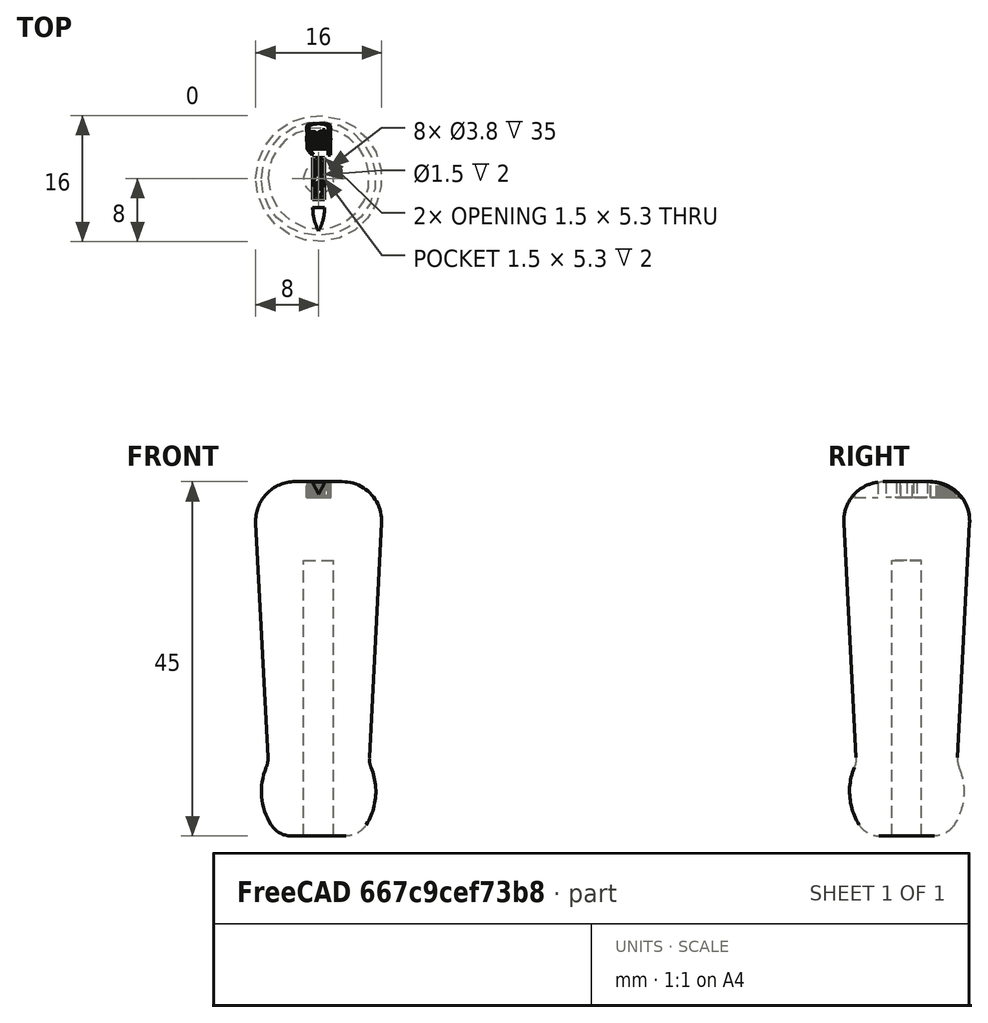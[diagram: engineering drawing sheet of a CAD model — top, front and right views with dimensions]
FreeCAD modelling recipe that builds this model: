
FCSTD DOCUMENT  (FreeCAD 1.0R39285 (Git))
Label:  NeedleFileHandle
License: All rights reserved
LicenseURL: https://en.wikipedia.org/wiki/All_rights_reserved
objects: PartDesign::CoordinateSystem×31, Sketcher::SketchObject×20, App::Part×11, Part::Part2DObjectPython×10, Part::Extrusion×10, PartDesign::Revolution×10, PartDesign::Pocket×10, PartDesign::Body×10, Part::Cut×10, App::Link×10, App::DocumentObjectGroup×3, App::FeaturePython×1, Spreadsheet::Sheet×1
note: 171 computed .brp shape members not serialized (recipe doc carries the construction recipe); baked Part::Feature solids carry a one-line shape summary decoded from their .brp

FEATURE [PartDesign::CoordinateSystem] LCS_Origin
  AttacherType = Attacher::AttachEngine3D
  AttachmentSupport = -> [X_Axis002]
  MapMode = 2
FEATURE [App::DocumentObjectGroup] Constraints
FEATURE [App::FeaturePython] Variables  # WARN: FeaturePython — macro-defined, semantics opaque (R4)
  Type = App::PropertyContainer
FEATURE [App::DocumentObjectGroup] Configurations
FEATURE [Spreadsheet::Sheet] Spreadsheet
  cells = A2='Nominal Hole Diameter; B2(NominalHoleDiameter)==3 mm; A3='Hole Tolerance; B3(HoleTolerance)==0.8 mm; A4='Hole Diameter; B4(HoleDiameter)==NominalHoleDiameter + HoleTolerance; A5='Hole Depth; B5(HoleDepth)==35 mm; A7='Bottom Flat Diameter; B7(BottomFlatDiameter)==7 mm; A9='Bottom Radius 1; B9(BottomRadius1)==3 mm; A10='Bottom Radius 2; B10(BottomRadius2)==8 mm; A11='Bottom Radius 3; B11(BottomRadius3)==BottomRadius1; A12='Top Radius; B12(TopRadius)==5 mm; A14='Top Flat Diameter; B14(TopFlatDiameter)==6 mm; A15='Top Solid Length; B15(TopSolidLength)==10 mm; A17='Bottom to Straight Height; B17(BottomToStraightHeight)==10 mm; A19='Lineup Distance; B19(LineupDistance)==20 mm; A21='Markings Depth
FEATURE [PartDesign::CoordinateSystem] LCS_Origin003
  AttacherType = Attacher::AttachEngine3D
  AttachmentSupport = -> [X_Axis006]
  MapMode = 2
FEATURE [Part::Part2DObjectPython] ShapeString002  # Draft 2D object (typed FeaturePython)
  FontFile = <userpath>/.fonts/ttf/arial.ttf
  Fuse = false
  Justification = 6
  JustificationReference = 0
  KeepLeftMargin = false
  MakeFace = true
  ObliqueAngle = 0
  ScaleToSize = true
  Size = 3
  String = 3
  Tracking = 0
FEATURE [Part::Extrusion] Extrude002  label="Text002"
  Base = -> ShapeString002
  Dir = (0,0,1)
  DirMode = 2
  FaceMakerClass = Part::FaceMakerBullseye
  FaceMakerMode = 3
  LengthFwd = 2
  LengthRev = 0
  Placement = pos=(1.5,4,43) rot=(0,0,1;1.5708rad)
  Solid = false
  Symmetric = false
FEATURE [Sketcher::SketchObject] Sketch004
  ArcFitTolerance = 1e-06
  AttachmentSupport = -> [XZ_Plane005]
  FullyConstrained = true
  MakeInternals = false
  MapMode = 5
  Placement = pos=(0,0,0) rot=(1,0,0;1.5708rad)
  expr: Constraints[10] = <<Spreadsheet>>.TopFlatDiameter / 2
  expr: Constraints[22] = <<Spreadsheet>>.TopRadius
  expr: Constraints[23] = <<Spreadsheet>>.BottomRadius1
  expr: Constraints[24] = <<Spreadsheet>>.BottomRadius2
  expr: Constraints[25] = <<Spreadsheet>>.BottomToStraightHeight
  expr: Constraints[26] = <<Spreadsheet>>.BottomFlatDiameter / 2
  expr: Constraints[27] = <<Spreadsheet>>.BottomRadius3
  expr: Constraints[5] = <<Spreadsheet>>.HoleDiameter / 2
  expr: Constraints[6] = <<Spreadsheet>>.HoleDepth
  expr: Constraints[7] = <<Spreadsheet>>.TopSolidLength
  sketch-geometry (10):
    g0: LineSegment StartX=-1.9 StartY=0 StartZ=0 EndX=-1.9 EndY=35 EndZ=0
    g1: LineSegment StartX=-1.9 StartY=35 StartZ=0 EndX=0 EndY=35 EndZ=0
    g2: LineSegment StartX=0 StartY=35 StartZ=0 EndX=0 EndY=45 EndZ=0
    g3: LineSegment StartX=0 StartY=45 StartZ=0 EndX=-3 EndY=45 EndZ=0
    g4: ArcOfCircle CenterX=-3 CenterY=40 CenterZ=0 NormalX=0 NormalY=0 NormalZ=1 AngleXU=0 Radius=5 StartAngle=1.5708 EndAngle=3.19395
    g5: LineSegment StartX=-1.9 StartY=0 StartZ=0 EndX=-3.5 EndY=0 EndZ=0
    g6: ArcOfCircle CenterX=-3.5 CenterY=3 CenterZ=0 NormalX=0 NormalY=0 NormalZ=1 AngleXU=0 Radius=3 StartAngle=3.70042 EndAngle=4.71239
    g7: ArcOfCircle CenterX=0.739385 CenterY=5.65096 CenterZ=0 NormalX=0 NormalY=0 NormalZ=1 AngleXU=0 Radius=8 StartAngle=2.75061 EndAngle=3.70042
    g8: ArcOfCircle CenterX=-9.43052 CenterY=9.84299 CenterZ=0 NormalX=0 NormalY=0 NormalZ=1 AngleXU=0 Radius=3 StartAngle=5.89221 EndAngle=6.33555
    g9: LineSegment StartX=-6.43463 StartY=10 StartZ=0 EndX=-7.99315 EndY=39.7383 EndZ=0
  constraints (28):
    c: PointOnObject(g0,g-1)
    c: Vertical(g0)
    c: Coincident(g0,g1)
    c: PointOnObject(g1,g-2)
    c: Horizontal(g1)
    c: DistanceX(g1,g1) = 1.9
    c: DistanceY(g0,g0) = 35
    c: Distance(g2) = 10
    c: Coincident(g2,g1)
    c: PointOnObject(g2,g-2)
    c: Distance(g3) = 3
    c: Coincident(g3,g2)
    c: Horizontal(g3)
    c: Coincident(g5,g0)
    c: PointOnObject(g5,g-1)
    c: Tangent(g6,g5) = 1.5708
    c: Tangent(g7,g6) = -1.5708
    c: Tangent(g8,g7) = 1.5708
    c: Tangent(g9,g8) = -1.5708
    c: Tangent(g4,g3) = -1.5708
    c: Tangent(g9,g4) = 1.5708
    c: Angle(g-2,g9) = 0.0523599
    c: Radius(g4) = 5
    c: Radius(g6) = 3
    c: Radius(g7) = 8
    c: DistanceY(g8) = 10
    c: DistanceX(g5,g-1) = 3.5
    c: Radius(g8) = 3
FEATURE [PartDesign::Revolution] Revolution002
  Angle = 360
  Angle2 = 60
  Axis = (0,2e-16,1)
  Base = (0,0,0)
  Placement = pos=(0,0,0) rot=(1,0,0;1.5708rad)
  Profile = -> Sketch004
  ReferenceAxis = -> Sketch004 [V_Axis]
  Refine = true
  Suppressed = false
  Type = 0
FEATURE [Sketcher::SketchObject] Sketch005
  ArcFitTolerance = 1e-06
  AttachmentSupport = -> [Revolution002]
  FullyConstrained = true
  MakeInternals = false
  MapMode = 5
  Placement = pos=(0,1e-14,45) rot=(0,0,1;3.14159rad)
  sketch-geometry (11):
    g0: LineSegment [constr] StartX=-0.75 StartY=-2.65 StartZ=0 EndX=0.75 EndY=-2.65 EndZ=0
    g1: LineSegment [constr] StartX=0.75 StartY=-2.65 StartZ=0 EndX=0.75 EndY=2.65 EndZ=0
    g2: LineSegment [constr] StartX=0.75 StartY=2.65 StartZ=0 EndX=-0.75 EndY=2.65 EndZ=0
    g3: LineSegment [constr] StartX=-0.75 StartY=2.65 StartZ=0 EndX=-0.75 EndY=-2.65 EndZ=0
    g4: GeomPoint [constr] X=0 Y=0 Z=0
    g5: LineSegment StartX=-0.75 StartY=3.65 StartZ=0 EndX=0.75 EndY=3.65 EndZ=0
    g6: ArcOfCircle CenterX=5.625 CenterY=3.65 CenterZ=0 NormalX=0 NormalY=0 NormalZ=1 AngleXU=0 Radius=6.375 StartAngle=2.65164 EndAngle=3.14159
    g7: ArcOfCircle CenterX=-5.625 CenterY=3.65 CenterZ=0 NormalX=0 NormalY=0 NormalZ=1 AngleXU=0 Radius=6.375 StartAngle=0 EndAngle=0.489957
    g8: ArcOfCircle CenterX=4.30667 CenterY=-7e-16 CenterZ=0 NormalX=0 NormalY=0 NormalZ=1 AngleXU=0 Radius=5.05667 StartAngle=2.58998 EndAngle=3.6932
    g9: ArcOfCircle CenterX=-4.30667 CenterY=7e-16 CenterZ=0 NormalX=0 NormalY=0 NormalZ=1 AngleXU=0 Radius=5.05667 StartAngle=5.73157 EndAngle=6.8348
    g10: GeomPoint X=0.75 Y=0 Z=0
  constraints (31):
    c: Coincident(g0,g1)
    c: Coincident(g1,g2)
    c: Coincident(g2,g3)
    c: Coincident(g3,g0)
    c: Horizontal(g0)
    c: Horizontal(g2)
    c: Vertical(g1)
    c: Vertical(g3)
    c: Symmetric(g2,g0,g4)
    c: Distance(g1,g3) = 1.5
    c: Distance(g0,g2) = 5.3
    c: Coincident(g4,g-1)
    c: Horizontal(g5)
    c: Coincident(g6,g5)
    c: PointOnObject(g6,g-2)
    c: Coincident(g7,g6)
    c: Coincident(g7,g5)
    c: Equal(g7,g6)
    c: Equal(g2,g5)
    c: Vertical(g5,g2)
    c: DistanceY(g1,g5) = 1
    c: DistanceY(g5,g6) = 3
    c: Perpendicular(g7,g5)
    c: Symmetric(g2,g2,g8)
    c: Symmetric(g0,g0,g8)
    c: Coincident(g9,g8)
    c: Coincident(g9,g8)
    c: PointOnObject(g10,g1)
    c: PointOnObject(g10,g9)
    c: PointOnObject(g10,g-1)
    c: Equal(g9,g8)
FEATURE [PartDesign::Pocket] Pocket002
  BaseFeature = -> Revolution002
  Direction = (0,0,-1)
  Length = 2
  Length2 = 5
  Placement = pos=(0,0,0) rot=(1,0,0;1.5708rad)
  Profile = -> Sketch005
  ReferenceAxis = -> Sketch005 [N_Axis]
  Refine = true
  Suppressed = false
  Type = 0
FEATURE [PartDesign::Body] Body002
  AllowCompound = false
  Group = -> [Sketch004,Revolution002,Sketch005,Pocket002]
  Origin = -> Origin005
  Tip = -> Pocket002
FEATURE [Part::Cut] Cut002
  Base = -> Body002
  Refine = true
  Tool = -> Extrude002
FEATURE [PartDesign::CoordinateSystem] Next002
  AttacherType = Attacher::AttachEngine3D
  AttachmentOffset = pos=(-20,0,0) rot=(0,0,1;3.14159rad)
  AttachmentSupport = -> [Cut002]
  MapMode = 11
  Placement = pos=(-4.2e-15,20,0) rot=(0,0,1;1.5708rad)
  expr: .AttachmentOffset.Base.x = -<<Spreadsheet>>.LineupDistance
FEATURE [PartDesign::CoordinateSystem] This002
  AttacherType = Attacher::AttachEngine3D
  AttachmentOffset = pos=(0,0,0) rot=(0,0,1;3.14159rad)
  AttachmentSupport = -> [Cut002]
  MapMode = 11
  Placement = pos=(2e-16,0,0) rot=(0,0,1;1.5708rad)
FEATURE [App::Part] Part001  label="3 - Dagger Rounded"
  Group = -> [LCS_Origin003,Body002,ShapeString002,Extrude002,Cut002,This002,Next002]
  Origin = -> Origin006
FEATURE [App::Link] ____Knife_Rounded  label="3 - Dagger Rounded001"
  AttachedBy = #This002
  AttachedTo = ____Flat_Straight#Next011
  LinkPlacement = pos=(40,-20,0) rot=(0,0,-1;1.5708rad)
  LinkedObject = -> Part001
  Placement = pos=(40,-20,0) rot=(0,0,-1;1.5708rad)
  SolverId = Asm4EE
  expr: Placement = ____Flat_Straight.Placement * Next011.Placement * AttachmentOffset * This002.Placement ^ -1
FEATURE [PartDesign::CoordinateSystem] LCS_Origin004
  AttacherType = Attacher::AttachEngine3D
  AttachmentSupport = -> [X_Axis008]
  MapMode = 2
FEATURE [Part::Part2DObjectPython] ShapeString003  # Draft 2D object (typed FeaturePython)
  FontFile = <userpath>/.fonts/ttf/arial.ttf
  Fuse = false
  Justification = 6
  JustificationReference = 0
  KeepLeftMargin = false
  MakeFace = true
  ObliqueAngle = 0
  ScaleToSize = true
  Size = 3
  String = 4
  Tracking = 0
FEATURE [Part::Extrusion] Extrude003  label="Text003"
  Base = -> ShapeString003
  Dir = (0,0,1)
  DirMode = 2
  FaceMakerClass = Part::FaceMakerBullseye
  FaceMakerMode = 3
  LengthFwd = 2
  LengthRev = 0
  Placement = pos=(1.5,4,43) rot=(0,0,1;1.5708rad)
  Solid = false
  Symmetric = false
FEATURE [Sketcher::SketchObject] Sketch006
  ArcFitTolerance = 1e-06
  AttachmentSupport = -> [XZ_Plane007]
  FullyConstrained = true
  MakeInternals = false
  MapMode = 5
  Placement = pos=(0,0,0) rot=(1,0,0;1.5708rad)
  expr: Constraints[10] = <<Spreadsheet>>.TopFlatDiameter / 2
  expr: Constraints[22] = <<Spreadsheet>>.TopRadius
  expr: Constraints[23] = <<Spreadsheet>>.BottomRadius1
  expr: Constraints[24] = <<Spreadsheet>>.BottomRadius2
  expr: Constraints[25] = <<Spreadsheet>>.BottomToStraightHeight
  expr: Constraints[26] = <<Spreadsheet>>.BottomFlatDiameter / 2
  expr: Constraints[27] = <<Spreadsheet>>.BottomRadius3
  expr: Constraints[5] = <<Spreadsheet>>.HoleDiameter / 2
  expr: Constraints[6] = <<Spreadsheet>>.HoleDepth
  expr: Constraints[7] = <<Spreadsheet>>.TopSolidLength
  sketch-geometry (10):
    g0: LineSegment StartX=-1.9 StartY=0 StartZ=0 EndX=-1.9 EndY=35 EndZ=0
    g1: LineSegment StartX=-1.9 StartY=35 StartZ=0 EndX=0 EndY=35 EndZ=0
    g2: LineSegment StartX=0 StartY=35 StartZ=0 EndX=0 EndY=45 EndZ=0
    g3: LineSegment StartX=0 StartY=45 StartZ=0 EndX=-3 EndY=45 EndZ=0
    g4: ArcOfCircle CenterX=-3 CenterY=40 CenterZ=0 NormalX=0 NormalY=0 NormalZ=1 AngleXU=0 Radius=5 StartAngle=1.5708 EndAngle=3.19395
    g5: LineSegment StartX=-1.9 StartY=0 StartZ=0 EndX=-3.5 EndY=0 EndZ=0
    g6: ArcOfCircle CenterX=-3.5 CenterY=3 CenterZ=0 NormalX=0 NormalY=0 NormalZ=1 AngleXU=0 Radius=3 StartAngle=3.70042 EndAngle=4.71239
    g7: ArcOfCircle CenterX=0.739385 CenterY=5.65096 CenterZ=0 NormalX=0 NormalY=0 NormalZ=1 AngleXU=0 Radius=8 StartAngle=2.75061 EndAngle=3.70042
    g8: ArcOfCircle CenterX=-9.43052 CenterY=9.84299 CenterZ=0 NormalX=0 NormalY=0 NormalZ=1 AngleXU=0 Radius=3 StartAngle=5.89221 EndAngle=6.33555
    g9: LineSegment StartX=-6.43463 StartY=10 StartZ=0 EndX=-7.99315 EndY=39.7383 EndZ=0
  constraints (28):
    c: PointOnObject(g0,g-1)
    c: Vertical(g0)
    c: Coincident(g0,g1)
    c: PointOnObject(g1,g-2)
    c: Horizontal(g1)
    c: DistanceX(g1,g1) = 1.9
    c: DistanceY(g0,g0) = 35
    c: Distance(g2) = 10
    c: Coincident(g2,g1)
    c: PointOnObject(g2,g-2)
    c: Distance(g3) = 3
    c: Coincident(g3,g2)
    c: Horizontal(g3)
    c: Coincident(g5,g0)
    c: PointOnObject(g5,g-1)
    c: Tangent(g6,g5) = 1.5708
    c: Tangent(g7,g6) = -1.5708
    c: Tangent(g8,g7) = 1.5708
    c: Tangent(g9,g8) = -1.5708
    c: Tangent(g4,g3) = -1.5708
    c: Tangent(g9,g4) = 1.5708
    c: Angle(g-2,g9) = 0.0523599
    c: Radius(g4) = 5
    c: Radius(g6) = 3
    c: Radius(g7) = 8
    c: DistanceY(g8) = 10
    c: DistanceX(g5,g-1) = 3.5
    c: Radius(g8) = 3
FEATURE [PartDesign::Revolution] Revolution003
  Angle = 360
  Angle2 = 60
  Axis = (0,2e-16,1)
  Base = (0,0,0)
  Placement = pos=(0,0,0) rot=(1,0,0;1.5708rad)
  Profile = -> Sketch006
  ReferenceAxis = -> Sketch006 [V_Axis]
  Refine = true
  Suppressed = false
  Type = 0
FEATURE [Sketcher::SketchObject] Sketch007
  ArcFitTolerance = 1e-06
  AttachmentSupport = -> [Revolution003]
  FullyConstrained = true
  MakeInternals = false
  MapMode = 5
  Placement = pos=(0,1e-14,45) rot=(0,0,1;3.14159rad)
  sketch-geometry (13):
    g0: LineSegment [constr] StartX=-0.75 StartY=-2.65 StartZ=0 EndX=0.75 EndY=-2.65 EndZ=0
    g1: LineSegment [constr] StartX=0.75 StartY=-2.65 StartZ=0 EndX=0.75 EndY=2.65 EndZ=0
    g2: LineSegment [constr] StartX=0.75 StartY=2.65 StartZ=0 EndX=-0.75 EndY=2.65 EndZ=0
    g3: LineSegment [constr] StartX=-0.75 StartY=2.65 StartZ=0 EndX=-0.75 EndY=-2.65 EndZ=0
    g4: GeomPoint [constr] X=0 Y=0 Z=0
    g5: LineSegment StartX=-0.75 StartY=3.65 StartZ=0 EndX=0.75 EndY=3.65 EndZ=0
    g6: ArcOfCircle CenterX=5.625 CenterY=3.65 CenterZ=0 NormalX=0 NormalY=0 NormalZ=1 AngleXU=0 Radius=6.375 StartAngle=2.65164 EndAngle=3.14159
    g7: ArcOfCircle CenterX=-5.625 CenterY=3.65 CenterZ=0 NormalX=0 NormalY=0 NormalZ=1 AngleXU=0 Radius=6.375 StartAngle=0 EndAngle=0.489957
    g8: GeomPoint X=0.75 Y=0 Z=0
    g9: ArcOfCircle CenterX=0.795417 CenterY=0 CenterZ=0 NormalX=0 NormalY=0 NormalZ=1 AngleXU=0 Radius=1.54542 StartAngle=2.11145 EndAngle=4.17174
    g10: ArcOfCircle CenterX=-0.795417 CenterY=0 CenterZ=0 NormalX=0 NormalY=0 NormalZ=1 AngleXU=0 Radius=1.54542 StartAngle=5.25304 EndAngle=7.31333
    g11: LineSegment [constr] StartX=1.393e-13 StartY=1.325 StartZ=0 EndX=0 EndY=2.65 EndZ=0
    g12: LineSegment [constr] StartX=1.393e-13 StartY=1.325 StartZ=0 EndX=0 EndY=0 EndZ=0
  constraints (36):
    c: Coincident(g0,g1)
    c: Coincident(g1,g2)
    c: Coincident(g2,g3)
    c: Coincident(g3,g0)
    c: Horizontal(g0)
    c: Horizontal(g2)
    c: Vertical(g1)
    c: Vertical(g3)
    c: Symmetric(g2,g0,g4)
    c: Distance(g1,g3) = 1.5
    c: Distance(g0,g2) = 5.3
    c: Coincident(g4,g-1)
    c: Horizontal(g5)
    c: Coincident(g6,g5)
    c: PointOnObject(g6,g-2)
    c: Coincident(g7,g6)
    c: Coincident(g7,g5)
    c: Equal(g7,g6)
    c: Equal(g2,g5)
    c: Vertical(g5,g2)
    c: DistanceY(g1,g5) = 1
    c: DistanceY(g5,g6) = 3
    c: Perpendicular(g7,g5)
    c: PointOnObject(g8,g1)
    c: PointOnObject(g8,g-1)
    c: PointOnObject(g9,g-2)
    c: Coincident(g10,g9)
    c: Coincident(g10,g9)
    c: PointOnObject(g8,g10)
    c: Symmetric(g9,g9,g4)
    c: Equal(g9,g10)
    c: Coincident(g11,g9)
    c: Symmetric(g2,g2,g11)
    c: Coincident(g12,g9)
    c: Coincident(g12,g4)
    c: Equal(g11,g12)
FEATURE [PartDesign::Pocket] Pocket003
  BaseFeature = -> Revolution003
  Direction = (0,0,-1)
  Length = 2
  Length2 = 5
  Placement = pos=(0,0,0) rot=(1,0,0;1.5708rad)
  Profile = -> Sketch007
  ReferenceAxis = -> Sketch007 [N_Axis]
  Refine = true
  Suppressed = false
  Type = 0
FEATURE [PartDesign::Body] Body003
  AllowCompound = false
  Group = -> [Sketch006,Revolution003,Sketch007,Pocket003]
  Origin = -> Origin007
  Tip = -> Pocket003
FEATURE [Part::Cut] Cut003
  Base = -> Body003
  Refine = true
  Tool = -> Extrude003
FEATURE [PartDesign::CoordinateSystem] Next003
  AttacherType = Attacher::AttachEngine3D
  AttachmentOffset = pos=(-20,0,0) rot=(0,0,1;3.14159rad)
  AttachmentSupport = -> [Cut003]
  MapMode = 11
  Placement = pos=(-4.2e-15,20,0) rot=(0,0,1;1.5708rad)
  expr: .AttachmentOffset.Base.x = -<<Spreadsheet>>.LineupDistance
FEATURE [PartDesign::CoordinateSystem] This003
  AttacherType = Attacher::AttachEngine3D
  AttachmentOffset = pos=(0,0,0) rot=(0,0,1;3.14159rad)
  AttachmentSupport = -> [Cut003]
  MapMode = 11
  Placement = pos=(2e-16,0,0) rot=(0,0,1;1.5708rad)
FEATURE [App::Part] Part002  label="4 - Dagger Rounded Small"
  Group = -> [LCS_Origin004,Body003,ShapeString003,Extrude003,Cut003,This003,Next003]
  Origin = -> Origin008
FEATURE [App::Link] ____Knife_Rounded_Small  label="4 - Dagger Rounded Small001"
  AttachedBy = #This003
  AttachedTo = ____Knife_Rounded#Next002
  LinkPlacement = pos=(60,-20,0) rot=(0,0,-1;1.5708rad)
  LinkedObject = -> Part002
  Placement = pos=(60,-20,0) rot=(0,0,-1;1.5708rad)
  SolverId = Asm4EE
  expr: Placement = ____Knife_Rounded.Placement * Next002.Placement * AttachmentOffset * This003.Placement ^ -1
FEATURE [PartDesign::CoordinateSystem] LCS_Origin005
  AttacherType = Attacher::AttachEngine3D
  AttachmentSupport = -> [X_Axis010]
  MapMode = 2
FEATURE [Part::Part2DObjectPython] ShapeString004  # Draft 2D object (typed FeaturePython)
  FontFile = <userpath>/.fonts/ttf/arial.ttf
  Fuse = false
  Justification = 6
  JustificationReference = 0
  KeepLeftMargin = false
  MakeFace = true
  ObliqueAngle = 0
  ScaleToSize = true
  Size = 3
  String = 5
  Tracking = 0
FEATURE [Part::Extrusion] Extrude004  label="Text004"
  Base = -> ShapeString004
  Dir = (0,0,1)
  DirMode = 2
  FaceMakerClass = Part::FaceMakerBullseye
  FaceMakerMode = 3
  LengthFwd = 2
  LengthRev = 0
  Placement = pos=(1.5,4,43) rot=(0,0,1;1.5708rad)
  Solid = false
  Symmetric = false
FEATURE [Sketcher::SketchObject] Sketch008
  ArcFitTolerance = 1e-06
  AttachmentSupport = -> [XZ_Plane009]
  FullyConstrained = true
  MakeInternals = false
  MapMode = 5
  Placement = pos=(0,0,0) rot=(1,0,0;1.5708rad)
  expr: Constraints[10] = <<Spreadsheet>>.TopFlatDiameter / 2
  expr: Constraints[22] = <<Spreadsheet>>.TopRadius
  expr: Constraints[23] = <<Spreadsheet>>.BottomRadius1
  expr: Constraints[24] = <<Spreadsheet>>.BottomRadius2
  expr: Constraints[25] = <<Spreadsheet>>.BottomToStraightHeight
  expr: Constraints[26] = <<Spreadsheet>>.BottomFlatDiameter / 2
  expr: Constraints[27] = <<Spreadsheet>>.BottomRadius3
  expr: Constraints[5] = <<Spreadsheet>>.HoleDiameter / 2
  expr: Constraints[6] = <<Spreadsheet>>.HoleDepth
  expr: Constraints[7] = <<Spreadsheet>>.TopSolidLength
  sketch-geometry (10):
    g0: LineSegment StartX=-1.9 StartY=0 StartZ=0 EndX=-1.9 EndY=35 EndZ=0
    g1: LineSegment StartX=-1.9 StartY=35 StartZ=0 EndX=0 EndY=35 EndZ=0
    g2: LineSegment StartX=0 StartY=35 StartZ=0 EndX=0 EndY=45 EndZ=0
    g3: LineSegment StartX=0 StartY=45 StartZ=0 EndX=-3 EndY=45 EndZ=0
    g4: ArcOfCircle CenterX=-3 CenterY=40 CenterZ=0 NormalX=0 NormalY=0 NormalZ=1 AngleXU=0 Radius=5 StartAngle=1.5708 EndAngle=3.19395
    g5: LineSegment StartX=-1.9 StartY=0 StartZ=0 EndX=-3.5 EndY=0 EndZ=0
    g6: ArcOfCircle CenterX=-3.5 CenterY=3 CenterZ=0 NormalX=0 NormalY=0 NormalZ=1 AngleXU=0 Radius=3 StartAngle=3.70042 EndAngle=4.71239
    g7: ArcOfCircle CenterX=0.739385 CenterY=5.65096 CenterZ=0 NormalX=0 NormalY=0 NormalZ=1 AngleXU=0 Radius=8 StartAngle=2.75061 EndAngle=3.70042
    g8: ArcOfCircle CenterX=-9.43052 CenterY=9.84299 CenterZ=0 NormalX=0 NormalY=0 NormalZ=1 AngleXU=0 Radius=3 StartAngle=5.89221 EndAngle=6.33555
    g9: LineSegment StartX=-6.43463 StartY=10 StartZ=0 EndX=-7.99315 EndY=39.7383 EndZ=0
  constraints (28):
    c: PointOnObject(g0,g-1)
    c: Vertical(g0)
    c: Coincident(g0,g1)
    c: PointOnObject(g1,g-2)
    c: Horizontal(g1)
    c: DistanceX(g1,g1) = 1.9
    c: DistanceY(g0,g0) = 35
    c: Distance(g2) = 10
    c: Coincident(g2,g1)
    c: PointOnObject(g2,g-2)
    c: Distance(g3) = 3
    c: Coincident(g3,g2)
    c: Horizontal(g3)
    c: Coincident(g5,g0)
    c: PointOnObject(g5,g-1)
    c: Tangent(g6,g5) = 1.5708
    c: Tangent(g7,g6) = -1.5708
    c: Tangent(g8,g7) = 1.5708
    c: Tangent(g9,g8) = -1.5708
    c: Tangent(g4,g3) = -1.5708
    c: Tangent(g9,g4) = 1.5708
    c: Angle(g-2,g9) = 0.0523599
    c: Radius(g4) = 5
    c: Radius(g6) = 3
    c: Radius(g7) = 8
    c: DistanceY(g8) = 10
    c: DistanceX(g5,g-1) = 3.5
    c: Radius(g8) = 3
FEATURE [PartDesign::Revolution] Revolution004
  Angle = 360
  Angle2 = 60
  Axis = (0,2e-16,1)
  Base = (0,0,0)
  Placement = pos=(0,0,0) rot=(1,0,0;1.5708rad)
  Profile = -> Sketch008
  ReferenceAxis = -> Sketch008 [V_Axis]
  Refine = true
  Suppressed = false
  Type = 0
FEATURE [Sketcher::SketchObject] Sketch009
  ArcFitTolerance = 1e-06
  AttachmentSupport = -> [Revolution004]
  FullyConstrained = true
  MakeInternals = false
  MapMode = 5
  Placement = pos=(0,1e-14,45) rot=(0,0,1;3.14159rad)
  sketch-geometry (12):
    g0: LineSegment [constr] StartX=-0.75 StartY=-2.65 StartZ=0 EndX=0.75 EndY=-2.65 EndZ=0
    g1: LineSegment [constr] StartX=0.75 StartY=-2.65 StartZ=0 EndX=0.75 EndY=2.65 EndZ=0
    g2: LineSegment [constr] StartX=0.75 StartY=2.65 StartZ=0 EndX=-0.75 EndY=2.65 EndZ=0
    g3: LineSegment [constr] StartX=-0.75 StartY=2.65 StartZ=0 EndX=-0.75 EndY=-2.65 EndZ=0
    g4: GeomPoint [constr] X=0 Y=0 Z=0
    g5: LineSegment StartX=-0.75 StartY=3.65 StartZ=0 EndX=0.75 EndY=3.65 EndZ=0
    g6: ArcOfCircle CenterX=5.625 CenterY=3.65 CenterZ=0 NormalX=0 NormalY=0 NormalZ=1 AngleXU=0 Radius=6.375 StartAngle=2.65164 EndAngle=3.14159
    g7: ArcOfCircle CenterX=-5.625 CenterY=3.65 CenterZ=0 NormalX=0 NormalY=0 NormalZ=1 AngleXU=0 Radius=6.375 StartAngle=1e-16 EndAngle=0.489957
    g8: GeomPoint X=0.75 Y=0 Z=0
    g9: LineSegment StartX=0.75 StartY=2.65 StartZ=0 EndX=0.75 EndY=-2.65 EndZ=0
    g10: LineSegment StartX=0.75 StartY=-2.65 StartZ=0 EndX=-0.75 EndY=0 EndZ=0
    g11: LineSegment StartX=-0.75 StartY=0 StartZ=0 EndX=0.75 EndY=2.65 EndZ=0
  constraints (31):
    c: Coincident(g0,g1)
    c: Coincident(g1,g2)
    c: Coincident(g2,g3)
    c: Coincident(g3,g0)
    c: Horizontal(g0)
    c: Horizontal(g2)
    c: Vertical(g1)
    c: Vertical(g3)
    c: Symmetric(g2,g0,g4)
    c: Distance(g1,g3) = 1.5
    c: Distance(g0,g2) = 5.3
    c: Coincident(g4,g-1)
    c: Horizontal(g5)
    c: Coincident(g6,g5)
    c: PointOnObject(g6,g-2)
    c: Coincident(g7,g6)
    c: Coincident(g7,g5)
    c: Equal(g7,g6)
    c: Equal(g2,g5)
    c: Vertical(g5,g2)
    c: DistanceY(g1,g5) = 1
    c: DistanceY(g5,g6) = 3
    c: Perpendicular(g7,g5)
    c: PointOnObject(g8,g1)
    c: PointOnObject(g8,g-1)
    c: Coincident(g9,g10)
    c: Symmetric(g3,g3,g10)
    c: Coincident(g10,g11)
    c: Coincident(g11,g9)
    c: Coincident(g9,g0)
    c: Coincident(g9,g1)
FEATURE [PartDesign::Pocket] Pocket004
  BaseFeature = -> Revolution004
  Direction = (0,0,-1)
  Length = 2
  Length2 = 5
  Placement = pos=(0,0,0) rot=(1,0,0;1.5708rad)
  Profile = -> Sketch009
  ReferenceAxis = -> Sketch009 [N_Axis]
  Refine = true
  Suppressed = false
  Type = 0
FEATURE [PartDesign::Body] Body004
  AllowCompound = false
  Group = -> [Sketch008,Revolution004,Sketch009,Pocket004]
  Origin = -> Origin009
  Tip = -> Pocket004
FEATURE [Part::Cut] Cut004
  Base = -> Body004
  Refine = true
  Tool = -> Extrude004
FEATURE [PartDesign::CoordinateSystem] Next004
  AttacherType = Attacher::AttachEngine3D
  AttachmentOffset = pos=(-20,0,0) rot=(0,0,1;3.14159rad)
  AttachmentSupport = -> [Cut004]
  MapMode = 11
  Placement = pos=(-4.2e-15,20,0) rot=(0,0,1;1.5708rad)
  expr: .AttachmentOffset.Base.x = -<<Spreadsheet>>.LineupDistance
FEATURE [PartDesign::CoordinateSystem] This004
  AttacherType = Attacher::AttachEngine3D
  AttachmentOffset = pos=(0,0,0) rot=(0,0,1;3.14159rad)
  AttachmentSupport = -> [Cut004]
  MapMode = 11
  Placement = pos=(2e-16,0,0) rot=(0,0,1;1.5708rad)
FEATURE [App::Part] Part003  label="5 - Triangle Flattened"
  Group = -> [LCS_Origin005,Body004,ShapeString004,Extrude004,Cut004,This004,Next004]
  Origin = -> Origin010
FEATURE [App::Link] ____Triangle_Flattened  label="5 - Triangle Flattened001"
  AttachedBy = #This004
  AttachedTo = ____Knife_Rounded_Small#Next003
  LinkPlacement = pos=(80,-20,0) rot=(0,0,-1;1.5708rad)
  LinkedObject = -> Part003
  Placement = pos=(80,-20,0) rot=(0,0,-1;1.5708rad)
  SolverId = Asm4EE
  expr: Placement = ____Knife_Rounded_Small.Placement * Next003.Placement * AttachmentOffset * This004.Placement ^ -1
FEATURE [PartDesign::CoordinateSystem] LCS_Origin006
  AttacherType = Attacher::AttachEngine3D
  AttachmentSupport = -> [X_Axis012]
  MapMode = 2
FEATURE [Part::Part2DObjectPython] ShapeString005  # Draft 2D object (typed FeaturePython)
  FontFile = <userpath>/.fonts/ttf/arial.ttf
  Fuse = false
  Justification = 6
  JustificationReference = 0
  KeepLeftMargin = false
  MakeFace = true
  ObliqueAngle = 0
  ScaleToSize = true
  Size = 3
  String = 6
  Tracking = 0
FEATURE [Part::Extrusion] Extrude005  label="Text005"
  Base = -> ShapeString005
  Dir = (0,0,1)
  DirMode = 2
  FaceMakerClass = Part::FaceMakerBullseye
  FaceMakerMode = 3
  LengthFwd = 2
  LengthRev = 0
  Placement = pos=(1.5,4,43) rot=(0,0,1;1.5708rad)
  Solid = false
  Symmetric = false
FEATURE [Sketcher::SketchObject] Sketch010
  ArcFitTolerance = 1e-06
  AttachmentSupport = -> [XZ_Plane011]
  FullyConstrained = true
  MakeInternals = false
  MapMode = 5
  Placement = pos=(0,0,0) rot=(1,0,0;1.5708rad)
  expr: Constraints[10] = <<Spreadsheet>>.TopFlatDiameter / 2
  expr: Constraints[22] = <<Spreadsheet>>.TopRadius
  expr: Constraints[23] = <<Spreadsheet>>.BottomRadius1
  expr: Constraints[24] = <<Spreadsheet>>.BottomRadius2
  expr: Constraints[25] = <<Spreadsheet>>.BottomToStraightHeight
  expr: Constraints[26] = <<Spreadsheet>>.BottomFlatDiameter / 2
  expr: Constraints[27] = <<Spreadsheet>>.BottomRadius3
  expr: Constraints[5] = <<Spreadsheet>>.HoleDiameter / 2
  expr: Constraints[6] = <<Spreadsheet>>.HoleDepth
  expr: Constraints[7] = <<Spreadsheet>>.TopSolidLength
  sketch-geometry (10):
    g0: LineSegment StartX=-1.9 StartY=0 StartZ=0 EndX=-1.9 EndY=35 EndZ=0
    g1: LineSegment StartX=-1.9 StartY=35 StartZ=0 EndX=0 EndY=35 EndZ=0
    g2: LineSegment StartX=0 StartY=35 StartZ=0 EndX=0 EndY=45 EndZ=0
    g3: LineSegment StartX=0 StartY=45 StartZ=0 EndX=-3 EndY=45 EndZ=0
    g4: ArcOfCircle CenterX=-3 CenterY=40 CenterZ=0 NormalX=0 NormalY=0 NormalZ=1 AngleXU=0 Radius=5 StartAngle=1.5708 EndAngle=3.19395
    g5: LineSegment StartX=-1.9 StartY=0 StartZ=0 EndX=-3.5 EndY=0 EndZ=0
    g6: ArcOfCircle CenterX=-3.5 CenterY=3 CenterZ=0 NormalX=0 NormalY=0 NormalZ=1 AngleXU=0 Radius=3 StartAngle=3.70042 EndAngle=4.71239
    g7: ArcOfCircle CenterX=0.739385 CenterY=5.65096 CenterZ=0 NormalX=0 NormalY=0 NormalZ=1 AngleXU=0 Radius=8 StartAngle=2.75061 EndAngle=3.70042
    g8: ArcOfCircle CenterX=-9.43052 CenterY=9.84299 CenterZ=0 NormalX=0 NormalY=0 NormalZ=1 AngleXU=0 Radius=3 StartAngle=5.89221 EndAngle=6.33555
    g9: LineSegment StartX=-6.43463 StartY=10 StartZ=0 EndX=-7.99315 EndY=39.7383 EndZ=0
  constraints (28):
    c: PointOnObject(g0,g-1)
    c: Vertical(g0)
    c: Coincident(g0,g1)
    c: PointOnObject(g1,g-2)
    c: Horizontal(g1)
    c: DistanceX(g1,g1) = 1.9
    c: DistanceY(g0,g0) = 35
    c: Distance(g2) = 10
    c: Coincident(g2,g1)
    c: PointOnObject(g2,g-2)
    c: Distance(g3) = 3
    c: Coincident(g3,g2)
    c: Horizontal(g3)
    c: Coincident(g5,g0)
    c: PointOnObject(g5,g-1)
    c: Tangent(g6,g5) = 1.5708
    c: Tangent(g7,g6) = -1.5708
    c: Tangent(g8,g7) = 1.5708
    c: Tangent(g9,g8) = -1.5708
    c: Tangent(g4,g3) = -1.5708
    c: Tangent(g9,g4) = 1.5708
    c: Angle(g-2,g9) = 0.0523599
    c: Radius(g4) = 5
    c: Radius(g6) = 3
    c: Radius(g7) = 8
    c: DistanceY(g8) = 10
    c: DistanceX(g5,g-1) = 3.5
    c: Radius(g8) = 3
FEATURE [PartDesign::Revolution] Revolution005
  Angle = 360
  Angle2 = 60
  Axis = (0,2e-16,1)
  Base = (0,0,0)
  Placement = pos=(0,0,0) rot=(1,0,0;1.5708rad)
  Profile = -> Sketch010
  ReferenceAxis = -> Sketch010 [V_Axis]
  Refine = true
  Suppressed = false
  Type = 0
FEATURE [Sketcher::SketchObject] Sketch011
  ArcFitTolerance = 1e-06
  AttachmentSupport = -> [Revolution005]
  FullyConstrained = true
  MakeInternals = false
  MapMode = 5
  Placement = pos=(0,1e-14,45) rot=(0,0,1;3.14159rad)
  sketch-geometry (12):
    g0: LineSegment [constr] StartX=-0.75 StartY=-2.65 StartZ=0 EndX=0.75 EndY=-2.65 EndZ=0
    g1: LineSegment [constr] StartX=0.75 StartY=-2.65 StartZ=0 EndX=0.75 EndY=2.65 EndZ=0
    g2: LineSegment [constr] StartX=0.75 StartY=2.65 StartZ=0 EndX=-0.75 EndY=2.65 EndZ=0
    g3: LineSegment [constr] StartX=-0.75 StartY=2.65 StartZ=0 EndX=-0.75 EndY=-2.65 EndZ=0
    g4: GeomPoint [constr] X=0 Y=0 Z=0
    g5: LineSegment StartX=-0.75 StartY=3.65 StartZ=0 EndX=0.75 EndY=3.65 EndZ=0
    g6: ArcOfCircle CenterX=5.625 CenterY=3.65 CenterZ=0 NormalX=0 NormalY=0 NormalZ=1 AngleXU=0 Radius=6.375 StartAngle=2.65164 EndAngle=3.14159
    g7: ArcOfCircle CenterX=-5.625 CenterY=3.65 CenterZ=0 NormalX=0 NormalY=0 NormalZ=1 AngleXU=0 Radius=6.375 StartAngle=0 EndAngle=0.489957
    g8: GeomPoint X=0.75 Y=0 Z=0
    g9: LineSegment StartX=-0.75 StartY=1.325 StartZ=0 EndX=0.75 EndY=1.325 EndZ=0
    g10: LineSegment StartX=0.75 StartY=1.325 StartZ=0 EndX=0 EndY=-2.65 EndZ=0
    g11: LineSegment StartX=0 StartY=-2.65 StartZ=0 EndX=-0.75 EndY=1.325 EndZ=0
  constraints (32):
    c: Coincident(g0,g1)
    c: Coincident(g1,g2)
    c: Coincident(g2,g3)
    c: Coincident(g3,g0)
    c: Horizontal(g0)
    c: Horizontal(g2)
    c: Vertical(g1)
    c: Vertical(g3)
    c: Symmetric(g2,g0,g4)
    c: Distance(g1,g3) = 1.5
    c: Distance(g0,g2) = 5.3
    c: Coincident(g4,g-1)
    c: Horizontal(g5)
    c: Coincident(g6,g5)
    c: PointOnObject(g6,g-2)
    c: Coincident(g7,g6)
    c: Coincident(g7,g5)
    c: Equal(g7,g6)
    c: Equal(g2,g5)
    c: Vertical(g5,g2)
    c: DistanceY(g1,g5) = 1
    c: DistanceY(g5,g6) = 3
    c: Perpendicular(g7,g5)
    c: PointOnObject(g8,g1)
    c: PointOnObject(g8,g-1)
    c: PointOnObject(g9,g3)
    c: Horizontal(g9)
    c: Coincident(g9,g10)
    c: Symmetric(g0,g0,g10)
    c: Coincident(g10,g11)
    c: Coincident(g11,g9)
    c: Symmetric(g8,g1,g9)
FEATURE [PartDesign::Pocket] Pocket005
  BaseFeature = -> Revolution005
  Direction = (0,0,-1)
  Length = 2
  Length2 = 5
  Placement = pos=(0,0,0) rot=(1,0,0;1.5708rad)
  Profile = -> Sketch011
  ReferenceAxis = -> Sketch011 [N_Axis]
  Refine = true
  Suppressed = false
  Type = 0
FEATURE [PartDesign::Body] Body005
  AllowCompound = false
  Group = -> [Sketch010,Revolution005,Sketch011,Pocket005]
  Origin = -> Origin011
  Tip = -> Pocket005
FEATURE [Part::Cut] Cut005
  Base = -> Body005
  Refine = true
  Tool = -> Extrude005
FEATURE [PartDesign::CoordinateSystem] Next005
  AttacherType = Attacher::AttachEngine3D
  AttachmentOffset = pos=(-20,0,0) rot=(0,0,1;3.14159rad)
  AttachmentSupport = -> [Cut005]
  MapMode = 11
  Placement = pos=(-4.2e-15,20,0) rot=(0,0,1;1.5708rad)
  expr: .AttachmentOffset.Base.x = -<<Spreadsheet>>.LineupDistance
FEATURE [PartDesign::CoordinateSystem] This005
  AttacherType = Attacher::AttachEngine3D
  AttachmentOffset = pos=(0,0,0) rot=(0,0,1;3.14159rad)
  AttachmentSupport = -> [Cut005]
  MapMode = 11
  Placement = pos=(2e-16,0,0) rot=(0,0,1;1.5708rad)
FEATURE [App::Part] Part004  label="6 - Knife"
  Group = -> [LCS_Origin006,Body005,ShapeString005,Extrude005,Cut005,This005,Next005]
  Origin = -> Origin012
FEATURE [App::Link] ____Sharp_Edge  label="6 - Knife001"
  AttachedBy = #This005
  AttachedTo = Parent Assembly#LCS_Origin
  AttachmentOffset = pos=(0,-40,0) rot=(0,0,1;0rad)
  LinkPlacement = pos=(0,-40,0) rot=(0,0,-1;1.5708rad)
  LinkedObject = -> Part004
  Placement = pos=(0,-40,0) rot=(0,0,-1;1.5708rad)
  SolverId = Asm4EE
  expr: Placement = LCS_Origin.Placement * AttachmentOffset * This005.Placement ^ -1
FEATURE [PartDesign::CoordinateSystem] LCS_Origin007
  AttacherType = Attacher::AttachEngine3D
  AttachmentSupport = -> [X_Axis014]
  MapMode = 2
FEATURE [Part::Part2DObjectPython] ShapeString006  # Draft 2D object (typed FeaturePython)
  FontFile = <userpath>/.fonts/ttf/arial.ttf
  Fuse = false
  Justification = 6
  JustificationReference = 0
  KeepLeftMargin = false
  MakeFace = true
  ObliqueAngle = 0
  ScaleToSize = true
  Size = 3
  String = 7
  Tracking = 0
FEATURE [Part::Extrusion] Extrude006  label="Text006"
  Base = -> ShapeString006
  Dir = (0,0,1)
  DirMode = 2
  FaceMakerClass = Part::FaceMakerBullseye
  FaceMakerMode = 3
  LengthFwd = 2
  LengthRev = 0
  Placement = pos=(1.5,4,43) rot=(0,0,1;1.5708rad)
  Solid = false
  Symmetric = false
FEATURE [Sketcher::SketchObject] Sketch012
  ArcFitTolerance = 1e-06
  AttachmentSupport = -> [XZ_Plane013]
  FullyConstrained = true
  MakeInternals = false
  MapMode = 5
  Placement = pos=(0,0,0) rot=(1,0,0;1.5708rad)
  expr: Constraints[10] = <<Spreadsheet>>.TopFlatDiameter / 2
  expr: Constraints[22] = <<Spreadsheet>>.TopRadius
  expr: Constraints[23] = <<Spreadsheet>>.BottomRadius1
  expr: Constraints[24] = <<Spreadsheet>>.BottomRadius2
  expr: Constraints[25] = <<Spreadsheet>>.BottomToStraightHeight
  expr: Constraints[26] = <<Spreadsheet>>.BottomFlatDiameter / 2
  expr: Constraints[27] = <<Spreadsheet>>.BottomRadius3
  expr: Constraints[5] = <<Spreadsheet>>.HoleDiameter / 2
  expr: Constraints[6] = <<Spreadsheet>>.HoleDepth
  expr: Constraints[7] = <<Spreadsheet>>.TopSolidLength
  sketch-geometry (10):
    g0: LineSegment StartX=-1.9 StartY=0 StartZ=0 EndX=-1.9 EndY=35 EndZ=0
    g1: LineSegment StartX=-1.9 StartY=35 StartZ=0 EndX=0 EndY=35 EndZ=0
    g2: LineSegment StartX=0 StartY=35 StartZ=0 EndX=0 EndY=45 EndZ=0
    g3: LineSegment StartX=0 StartY=45 StartZ=0 EndX=-3 EndY=45 EndZ=0
    g4: ArcOfCircle CenterX=-3 CenterY=40 CenterZ=0 NormalX=0 NormalY=0 NormalZ=1 AngleXU=0 Radius=5 StartAngle=1.5708 EndAngle=3.19395
    g5: LineSegment StartX=-1.9 StartY=0 StartZ=0 EndX=-3.5 EndY=0 EndZ=0
    g6: ArcOfCircle CenterX=-3.5 CenterY=3 CenterZ=0 NormalX=0 NormalY=0 NormalZ=1 AngleXU=0 Radius=3 StartAngle=3.70042 EndAngle=4.71239
    g7: ArcOfCircle CenterX=0.739385 CenterY=5.65096 CenterZ=0 NormalX=0 NormalY=0 NormalZ=1 AngleXU=0 Radius=8 StartAngle=2.75061 EndAngle=3.70042
    g8: ArcOfCircle CenterX=-9.43052 CenterY=9.84299 CenterZ=0 NormalX=0 NormalY=0 NormalZ=1 AngleXU=0 Radius=3 StartAngle=5.89221 EndAngle=6.33555
    g9: LineSegment StartX=-6.43463 StartY=10 StartZ=0 EndX=-7.99315 EndY=39.7383 EndZ=0
  constraints (28):
    c: PointOnObject(g0,g-1)
    c: Vertical(g0)
    c: Coincident(g0,g1)
    c: PointOnObject(g1,g-2)
    c: Horizontal(g1)
    c: DistanceX(g1,g1) = 1.9
    c: DistanceY(g0,g0) = 35
    c: Distance(g2) = 10
    c: Coincident(g2,g1)
    c: PointOnObject(g2,g-2)
    c: Distance(g3) = 3
    c: Coincident(g3,g2)
    c: Horizontal(g3)
    c: Coincident(g5,g0)
    c: PointOnObject(g5,g-1)
    c: Tangent(g6,g5) = 1.5708
    c: Tangent(g7,g6) = -1.5708
    c: Tangent(g8,g7) = 1.5708
    c: Tangent(g9,g8) = -1.5708
    c: Tangent(g4,g3) = -1.5708
    c: Tangent(g9,g4) = 1.5708
    c: Angle(g-2,g9) = 0.0523599
    c: Radius(g4) = 5
    c: Radius(g6) = 3
    c: Radius(g7) = 8
    c: DistanceY(g8) = 10
    c: DistanceX(g5,g-1) = 3.5
    c: Radius(g8) = 3
FEATURE [PartDesign::Revolution] Revolution006
  Angle = 360
  Angle2 = 60
  Axis = (0,2e-16,1)
  Base = (0,0,0)
  Placement = pos=(0,0,0) rot=(1,0,0;1.5708rad)
  Profile = -> Sketch012
  ReferenceAxis = -> Sketch012 [V_Axis]
  Refine = true
  Suppressed = false
  Type = 0
FEATURE [Sketcher::SketchObject] Sketch013
  ArcFitTolerance = 1e-06
  AttachmentSupport = -> [Revolution006]
  FullyConstrained = true
  MakeInternals = false
  MapMode = 5
  Placement = pos=(0,1e-14,45) rot=(0,0,1;3.14159rad)
  sketch-geometry (10):
    g0: LineSegment [constr] StartX=-0.75 StartY=-2.65 StartZ=0 EndX=0.75 EndY=-2.65 EndZ=0
    g1: LineSegment [constr] StartX=0.75 StartY=-2.65 StartZ=0 EndX=0.75 EndY=2.65 EndZ=0
    g2: LineSegment [constr] StartX=0.75 StartY=2.65 StartZ=0 EndX=-0.75 EndY=2.65 EndZ=0
    g3: LineSegment [constr] StartX=-0.75 StartY=2.65 StartZ=0 EndX=-0.75 EndY=-2.65 EndZ=0
    g4: GeomPoint [constr] X=0 Y=0 Z=0
    g5: LineSegment StartX=-0.75 StartY=3.65 StartZ=0 EndX=0.75 EndY=3.65 EndZ=0
    g6: ArcOfCircle CenterX=5.625 CenterY=3.65 CenterZ=0 NormalX=0 NormalY=0 NormalZ=1 AngleXU=0 Radius=6.375 StartAngle=2.65164 EndAngle=3.14159
    g7: ArcOfCircle CenterX=-5.625 CenterY=3.65 CenterZ=0 NormalX=0 NormalY=0 NormalZ=1 AngleXU=0 Radius=6.375 StartAngle=0 EndAngle=0.489957
    g8: GeomPoint X=0.75 Y=0 Z=0
    g9: Circle CenterX=0 CenterY=0 CenterZ=0 NormalX=0 NormalY=0 NormalZ=1 AngleXU=0 Radius=0.75
  constraints (27):
    c: Coincident(g0,g1)
    c: Coincident(g1,g2)
    c: Coincident(g2,g3)
    c: Coincident(g3,g0)
    c: Horizontal(g0)
    c: Horizontal(g2)
    c: Vertical(g1)
    c: Vertical(g3)
    c: Symmetric(g2,g0,g4)
    c: Distance(g1,g3) = 1.5
    c: Distance(g0,g2) = 5.3
    c: Coincident(g4,g-1)
    c: Horizontal(g5)
    c: Coincident(g6,g5)
    c: PointOnObject(g6,g-2)
    c: Coincident(g7,g6)
    c: Coincident(g7,g5)
    c: Equal(g7,g6)
    c: Equal(g2,g5)
    c: Vertical(g5,g2)
    c: DistanceY(g1,g5) = 1
    c: DistanceY(g5,g6) = 3
    c: Perpendicular(g7,g5)
    c: PointOnObject(g8,g1)
    c: PointOnObject(g8,g-1)
    c: Coincident(g9,g4)
    c: PointOnObject(g8,g9)
FEATURE [PartDesign::Pocket] Pocket006
  BaseFeature = -> Revolution006
  Direction = (0,0,-1)
  Length = 2
  Length2 = 5
  Placement = pos=(0,0,0) rot=(1,0,0;1.5708rad)
  Profile = -> Sketch013
  ReferenceAxis = -> Sketch013 [N_Axis]
  Refine = true
  Suppressed = false
  Type = 0
FEATURE [PartDesign::Body] Body006
  AllowCompound = false
  Group = -> [Sketch012,Revolution006,Sketch013,Pocket006]
  Origin = -> Origin013
  Tip = -> Pocket006
FEATURE [Part::Cut] Cut006
  Base = -> Body006
  Refine = true
  Tool = -> Extrude006
FEATURE [PartDesign::CoordinateSystem] Next006
  AttacherType = Attacher::AttachEngine3D
  AttachmentOffset = pos=(-20,0,0) rot=(0,0,1;3.14159rad)
  AttachmentSupport = -> [Cut006]
  MapMode = 11
  Placement = pos=(-4.2e-15,20,0) rot=(0,0,1;1.5708rad)
  expr: .AttachmentOffset.Base.x = -<<Spreadsheet>>.LineupDistance
FEATURE [PartDesign::CoordinateSystem] This006
  AttacherType = Attacher::AttachEngine3D
  AttachmentOffset = pos=(0,0,0) rot=(0,0,1;3.14159rad)
  AttachmentSupport = -> [Cut006]
  MapMode = 11
  Placement = pos=(2e-16,0,0) rot=(0,0,1;1.5708rad)
FEATURE [App::Part] Part005  label="7 - Round"
  Group = -> [LCS_Origin007,Body006,ShapeString006,Extrude006,Cut006,This006,Next006]
  Origin = -> Origin014
FEATURE [App::Link] ____Round  label="7 - Round001"
  AttachedBy = #This006
  AttachedTo = ____Sharp_Edge#Next005
  LinkPlacement = pos=(20,-40,0) rot=(0,0,-1;1.5708rad)
  LinkedObject = -> Part005
  Placement = pos=(20,-40,0) rot=(0,0,-1;1.5708rad)
  SolverId = Asm4EE
  expr: Placement = ____Sharp_Edge.Placement * Next005.Placement * AttachmentOffset * This006.Placement ^ -1
FEATURE [PartDesign::CoordinateSystem] LCS_Origin008
  AttacherType = Attacher::AttachEngine3D
  AttachmentSupport = -> [X_Axis016]
  MapMode = 2
FEATURE [Part::Part2DObjectPython] ShapeString007  # Draft 2D object (typed FeaturePython)
  FontFile = <userpath>/.fonts/ttf/arial.ttf
  Fuse = false
  Justification = 6
  JustificationReference = 0
  KeepLeftMargin = false
  MakeFace = true
  ObliqueAngle = 0
  ScaleToSize = true
  Size = 3
  String = 8
  Tracking = 0
FEATURE [Part::Extrusion] Extrude007  label="Text007"
  Base = -> ShapeString007
  Dir = (0,0,1)
  DirMode = 2
  FaceMakerClass = Part::FaceMakerBullseye
  FaceMakerMode = 3
  LengthFwd = 2
  LengthRev = 0
  Placement = pos=(1.5,4,43) rot=(0,0,1;1.5708rad)
  Solid = false
  Symmetric = false
FEATURE [Sketcher::SketchObject] Sketch014
  ArcFitTolerance = 1e-06
  AttachmentSupport = -> [XZ_Plane015]
  FullyConstrained = true
  MakeInternals = false
  MapMode = 5
  Placement = pos=(0,0,0) rot=(1,0,0;1.5708rad)
  expr: Constraints[10] = <<Spreadsheet>>.TopFlatDiameter / 2
  expr: Constraints[22] = <<Spreadsheet>>.TopRadius
  expr: Constraints[23] = <<Spreadsheet>>.BottomRadius1
  expr: Constraints[24] = <<Spreadsheet>>.BottomRadius2
  expr: Constraints[25] = <<Spreadsheet>>.BottomToStraightHeight
  expr: Constraints[26] = <<Spreadsheet>>.BottomFlatDiameter / 2
  expr: Constraints[27] = <<Spreadsheet>>.BottomRadius3
  expr: Constraints[5] = <<Spreadsheet>>.HoleDiameter / 2
  expr: Constraints[6] = <<Spreadsheet>>.HoleDepth
  expr: Constraints[7] = <<Spreadsheet>>.TopSolidLength
  sketch-geometry (10):
    g0: LineSegment StartX=-1.9 StartY=0 StartZ=0 EndX=-1.9 EndY=35 EndZ=0
    g1: LineSegment StartX=-1.9 StartY=35 StartZ=0 EndX=0 EndY=35 EndZ=0
    g2: LineSegment StartX=0 StartY=35 StartZ=0 EndX=0 EndY=45 EndZ=0
    g3: LineSegment StartX=0 StartY=45 StartZ=0 EndX=-3 EndY=45 EndZ=0
    g4: ArcOfCircle CenterX=-3 CenterY=40 CenterZ=0 NormalX=0 NormalY=0 NormalZ=1 AngleXU=0 Radius=5 StartAngle=1.5708 EndAngle=3.19395
    g5: LineSegment StartX=-1.9 StartY=0 StartZ=0 EndX=-3.5 EndY=0 EndZ=0
    g6: ArcOfCircle CenterX=-3.5 CenterY=3 CenterZ=0 NormalX=0 NormalY=0 NormalZ=1 AngleXU=0 Radius=3 StartAngle=3.70042 EndAngle=4.71239
    g7: ArcOfCircle CenterX=0.739385 CenterY=5.65096 CenterZ=0 NormalX=0 NormalY=0 NormalZ=1 AngleXU=0 Radius=8 StartAngle=2.75061 EndAngle=3.70042
    g8: ArcOfCircle CenterX=-9.43052 CenterY=9.84299 CenterZ=0 NormalX=0 NormalY=0 NormalZ=1 AngleXU=0 Radius=3 StartAngle=5.89221 EndAngle=6.33555
    g9: LineSegment StartX=-6.43463 StartY=10 StartZ=0 EndX=-7.99315 EndY=39.7383 EndZ=0
  constraints (28):
    c: PointOnObject(g0,g-1)
    c: Vertical(g0)
    c: Coincident(g0,g1)
    c: PointOnObject(g1,g-2)
    c: Horizontal(g1)
    c: DistanceX(g1,g1) = 1.9
    c: DistanceY(g0,g0) = 35
    c: Distance(g2) = 10
    c: Coincident(g2,g1)
    c: PointOnObject(g2,g-2)
    c: Distance(g3) = 3
    c: Coincident(g3,g2)
    c: Horizontal(g3)
    c: Coincident(g5,g0)
    c: PointOnObject(g5,g-1)
    c: Tangent(g6,g5) = 1.5708
    c: Tangent(g7,g6) = -1.5708
    c: Tangent(g8,g7) = 1.5708
    c: Tangent(g9,g8) = -1.5708
    c: Tangent(g4,g3) = -1.5708
    c: Tangent(g9,g4) = 1.5708
    c: Angle(g-2,g9) = 0.0523599
    c: Radius(g4) = 5
    c: Radius(g6) = 3
    c: Radius(g7) = 8
    c: DistanceY(g8) = 10
    c: DistanceX(g5,g-1) = 3.5
    c: Radius(g8) = 3
FEATURE [PartDesign::Revolution] Revolution007
  Angle = 360
  Angle2 = 60
  Axis = (0,2e-16,1)
  Base = (0,0,0)
  Placement = pos=(0,0,0) rot=(1,0,0;1.5708rad)
  Profile = -> Sketch014
  ReferenceAxis = -> Sketch014 [V_Axis]
  Refine = true
  Suppressed = false
  Type = 0
FEATURE [Sketcher::SketchObject] Sketch015
  ArcFitTolerance = 1e-06
  AttachmentSupport = -> [Revolution007]
  FullyConstrained = true
  MakeInternals = false
  MapMode = 5
  Placement = pos=(0,1e-14,45) rot=(0,0,1;3.14159rad)
  sketch-geometry (12):
    g0: LineSegment [constr] StartX=-0.75 StartY=-2.65 StartZ=0 EndX=0.75 EndY=-2.65 EndZ=0
    g1: LineSegment [constr] StartX=0.75 StartY=-2.65 StartZ=0 EndX=0.75 EndY=2.65 EndZ=0
    g2: LineSegment [constr] StartX=0.75 StartY=2.65 StartZ=0 EndX=-0.75 EndY=2.65 EndZ=0
    g3: LineSegment [constr] StartX=-0.75 StartY=2.65 StartZ=0 EndX=-0.75 EndY=-2.65 EndZ=0
    g4: GeomPoint [constr] X=0 Y=0 Z=0
    g5: LineSegment StartX=-0.75 StartY=3.65 StartZ=0 EndX=0.75 EndY=3.65 EndZ=0
    g6: ArcOfCircle CenterX=5.625 CenterY=3.65 CenterZ=0 NormalX=0 NormalY=0 NormalZ=1 AngleXU=0 Radius=6.375 StartAngle=2.65164 EndAngle=3.14159
    g7: ArcOfCircle CenterX=-5.625 CenterY=3.65 CenterZ=0 NormalX=0 NormalY=0 NormalZ=1 AngleXU=0 Radius=6.375 StartAngle=0 EndAngle=0.489957
    g8: GeomPoint X=0.75 Y=0 Z=0
    g9: LineSegment StartX=-0.75 StartY=1e-16 StartZ=0 EndX=0.75 EndY=0.866025 EndZ=0
    g10: LineSegment StartX=0.75 StartY=0.866025 StartZ=0 EndX=0.75 EndY=-0.866025 EndZ=0
    g11: LineSegment StartX=0.75 StartY=-0.866025 StartZ=0 EndX=-0.75 EndY=1e-16 EndZ=0
  constraints (33):
    c: Coincident(g0,g1)
    c: Coincident(g1,g2)
    c: Coincident(g2,g3)
    c: Coincident(g3,g0)
    c: Horizontal(g0)
    c: Horizontal(g2)
    c: Vertical(g1)
    c: Vertical(g3)
    c: Symmetric(g2,g0,g4)
    c: Distance(g1,g3) = 1.5
    c: Distance(g0,g2) = 5.3
    c: Coincident(g4,g-1)
    c: Horizontal(g5)
    c: Coincident(g6,g5)
    c: PointOnObject(g6,g-2)
    c: Coincident(g7,g6)
    c: Coincident(g7,g5)
    c: Equal(g7,g6)
    c: Equal(g2,g5)
    c: Vertical(g5,g2)
    c: DistanceY(g1,g5) = 1
    c: DistanceY(g5,g6) = 3
    c: Perpendicular(g7,g5)
    c: PointOnObject(g8,g1)
    c: PointOnObject(g8,g-1)
    c: Symmetric(g3,g3,g9)
    c: PointOnObject(g9,g1)
    c: Coincident(g9,g10)
    c: PointOnObject(g10,g1)
    c: Coincident(g10,g11)
    c: Coincident(g11,g9)
    c: Equal(g9,g10)
    c: Equal(g10,g11)
FEATURE [PartDesign::Pocket] Pocket007
  BaseFeature = -> Revolution007
  Direction = (0,0,-1)
  Length = 2
  Length2 = 5
  Placement = pos=(0,0,0) rot=(1,0,0;1.5708rad)
  Profile = -> Sketch015
  ReferenceAxis = -> Sketch015 [N_Axis]
  Refine = true
  Suppressed = false
  Type = 0
FEATURE [PartDesign::Body] Body007
  AllowCompound = false
  Group = -> [Sketch014,Revolution007,Sketch015,Pocket007]
  Origin = -> Origin015
  Tip = -> Pocket007
FEATURE [Part::Cut] Cut007
  Base = -> Body007
  Refine = true
  Tool = -> Extrude007
FEATURE [PartDesign::CoordinateSystem] Next007
  AttacherType = Attacher::AttachEngine3D
  AttachmentOffset = pos=(-20,0,0) rot=(0,0,1;3.14159rad)
  AttachmentSupport = -> [Cut007]
  MapMode = 11
  Placement = pos=(-4.2e-15,20,0) rot=(0,0,1;1.5708rad)
  expr: .AttachmentOffset.Base.x = -<<Spreadsheet>>.LineupDistance
FEATURE [PartDesign::CoordinateSystem] This007
  AttacherType = Attacher::AttachEngine3D
  AttachmentOffset = pos=(0,0,0) rot=(0,0,1;3.14159rad)
  AttachmentSupport = -> [Cut007]
  MapMode = 11
  Placement = pos=(2e-16,0,0) rot=(0,0,1;1.5708rad)
FEATURE [App::Part] Part006  label="8 - Triangle"
  Group = -> [LCS_Origin008,Body007,ShapeString007,Extrude007,Cut007,This007,Next007]
  Origin = -> Origin016
FEATURE [App::Link] ____Triangle  label="8 - Triangle001"
  AttachedBy = #This007
  AttachedTo = ____Round#Next006
  LinkPlacement = pos=(40,-40,0) rot=(0,0,-1;1.5708rad)
  LinkedObject = -> Part006
  Placement = pos=(40,-40,0) rot=(0,0,-1;1.5708rad)
  SolverId = Asm4EE
  expr: Placement = ____Round.Placement * Next006.Placement * AttachmentOffset * This007.Placement ^ -1
FEATURE [PartDesign::CoordinateSystem] LCS_Origin009
  AttacherType = Attacher::AttachEngine3D
  AttachmentSupport = -> [X_Axis018]
  MapMode = 2
FEATURE [Part::Part2DObjectPython] ShapeString008  # Draft 2D object (typed FeaturePython)
  FontFile = <userpath>/.fonts/ttf/arial.ttf
  Fuse = false
  Justification = 6
  JustificationReference = 0
  KeepLeftMargin = false
  MakeFace = true
  ObliqueAngle = 0
  ScaleToSize = true
  Size = 3
  String = 9
  Tracking = 0
FEATURE [Part::Extrusion] Extrude008  label="Text008"
  Base = -> ShapeString008
  Dir = (0,0,1)
  DirMode = 2
  FaceMakerClass = Part::FaceMakerBullseye
  FaceMakerMode = 3
  LengthFwd = 2
  LengthRev = 0
  Placement = pos=(1.5,4,43) rot=(0,0,1;1.5708rad)
  Solid = false
  Symmetric = false
FEATURE [Sketcher::SketchObject] Sketch016
  ArcFitTolerance = 1e-06
  AttachmentSupport = -> [XZ_Plane017]
  FullyConstrained = true
  MakeInternals = false
  MapMode = 5
  Placement = pos=(0,0,0) rot=(1,0,0;1.5708rad)
  expr: Constraints[10] = <<Spreadsheet>>.TopFlatDiameter / 2
  expr: Constraints[22] = <<Spreadsheet>>.TopRadius
  expr: Constraints[23] = <<Spreadsheet>>.BottomRadius1
  expr: Constraints[24] = <<Spreadsheet>>.BottomRadius2
  expr: Constraints[25] = <<Spreadsheet>>.BottomToStraightHeight
  expr: Constraints[26] = <<Spreadsheet>>.BottomFlatDiameter / 2
  expr: Constraints[27] = <<Spreadsheet>>.BottomRadius3
  expr: Constraints[5] = <<Spreadsheet>>.HoleDiameter / 2
  expr: Constraints[6] = <<Spreadsheet>>.HoleDepth
  expr: Constraints[7] = <<Spreadsheet>>.TopSolidLength
  sketch-geometry (10):
    g0: LineSegment StartX=-1.9 StartY=0 StartZ=0 EndX=-1.9 EndY=35 EndZ=0
    g1: LineSegment StartX=-1.9 StartY=35 StartZ=0 EndX=0 EndY=35 EndZ=0
    g2: LineSegment StartX=0 StartY=35 StartZ=0 EndX=0 EndY=45 EndZ=0
    g3: LineSegment StartX=0 StartY=45 StartZ=0 EndX=-3 EndY=45 EndZ=0
    g4: ArcOfCircle CenterX=-3 CenterY=40 CenterZ=0 NormalX=0 NormalY=0 NormalZ=1 AngleXU=0 Radius=5 StartAngle=1.5708 EndAngle=3.19395
    g5: LineSegment StartX=-1.9 StartY=0 StartZ=0 EndX=-3.5 EndY=0 EndZ=0
    g6: ArcOfCircle CenterX=-3.5 CenterY=3 CenterZ=0 NormalX=0 NormalY=0 NormalZ=1 AngleXU=0 Radius=3 StartAngle=3.70042 EndAngle=4.71239
    g7: ArcOfCircle CenterX=0.739385 CenterY=5.65096 CenterZ=0 NormalX=0 NormalY=0 NormalZ=1 AngleXU=0 Radius=8 StartAngle=2.75061 EndAngle=3.70042
    g8: ArcOfCircle CenterX=-9.43052 CenterY=9.84299 CenterZ=0 NormalX=0 NormalY=0 NormalZ=1 AngleXU=0 Radius=3 StartAngle=5.89221 EndAngle=6.33555
    g9: LineSegment StartX=-6.43463 StartY=10 StartZ=0 EndX=-7.99315 EndY=39.7383 EndZ=0
  constraints (28):
    c: PointOnObject(g0,g-1)
    c: Vertical(g0)
    c: Coincident(g0,g1)
    c: PointOnObject(g1,g-2)
    c: Horizontal(g1)
    c: DistanceX(g1,g1) = 1.9
    c: DistanceY(g0,g0) = 35
    c: Distance(g2) = 10
    c: Coincident(g2,g1)
    c: PointOnObject(g2,g-2)
    c: Distance(g3) = 3
    c: Coincident(g3,g2)
    c: Horizontal(g3)
    c: Coincident(g5,g0)
    c: PointOnObject(g5,g-1)
    c: Tangent(g6,g5) = 1.5708
    c: Tangent(g7,g6) = -1.5708
    c: Tangent(g8,g7) = 1.5708
    c: Tangent(g9,g8) = -1.5708
    c: Tangent(g4,g3) = -1.5708
    c: Tangent(g9,g4) = 1.5708
    c: Angle(g-2,g9) = 0.0523599
    c: Radius(g4) = 5
    c: Radius(g6) = 3
    c: Radius(g7) = 8
    c: DistanceY(g8) = 10
    c: DistanceX(g5,g-1) = 3.5
    c: Radius(g8) = 3
FEATURE [PartDesign::Revolution] Revolution008
  Angle = 360
  Angle2 = 60
  Axis = (0,2e-16,1)
  Base = (0,0,0)
  Placement = pos=(0,0,0) rot=(1,0,0;1.5708rad)
  Profile = -> Sketch016
  ReferenceAxis = -> Sketch016 [V_Axis]
  Refine = true
  Suppressed = false
  Type = 0
FEATURE [Sketcher::SketchObject] Sketch017
  ArcFitTolerance = 1e-06
  AttachmentSupport = -> [Revolution008]
  FullyConstrained = true
  MakeInternals = false
  MapMode = 5
  Placement = pos=(0,1e-14,45) rot=(0,0,1;3.14159rad)
  sketch-geometry (14):
    g0: LineSegment [constr] StartX=-0.75 StartY=-2.65 StartZ=0 EndX=0.75 EndY=-2.65 EndZ=0
    g1: LineSegment [constr] StartX=0.75 StartY=-2.65 StartZ=0 EndX=0.75 EndY=2.65 EndZ=0
    g2: LineSegment [constr] StartX=0.75 StartY=2.65 StartZ=0 EndX=-0.75 EndY=2.65 EndZ=0
    g3: LineSegment [constr] StartX=-0.75 StartY=2.65 StartZ=0 EndX=-0.75 EndY=-2.65 EndZ=0
    g4: GeomPoint [constr] X=0 Y=0 Z=0
    g5: LineSegment StartX=-0.75 StartY=3.65 StartZ=0 EndX=0.75 EndY=3.65 EndZ=0
    g6: ArcOfCircle CenterX=5.625 CenterY=3.65 CenterZ=0 NormalX=0 NormalY=0 NormalZ=1 AngleXU=0 Radius=6.375 StartAngle=2.65164 EndAngle=3.14159
    g7: ArcOfCircle CenterX=-5.625 CenterY=3.65 CenterZ=0 NormalX=0 NormalY=0 NormalZ=1 AngleXU=0 Radius=6.375 StartAngle=0 EndAngle=0.489957
    g8: GeomPoint X=0.75 Y=0 Z=0
    g9: LineSegment StartX=-0.75 StartY=0.75 StartZ=0 EndX=-0.75 EndY=-0.75 EndZ=0
    g10: LineSegment StartX=-0.75 StartY=-0.75 StartZ=0 EndX=0.75 EndY=-0.75 EndZ=0
    g11: LineSegment StartX=0.75 StartY=-0.75 StartZ=0 EndX=0.75 EndY=0.75 EndZ=0
    g12: LineSegment StartX=0.75 StartY=0.75 StartZ=0 EndX=-0.75 EndY=0.75 EndZ=0
    g13: GeomPoint [constr] X=0 Y=0 Z=0
  constraints (37):
    c: Coincident(g0,g1)
    c: Coincident(g1,g2)
    c: Coincident(g2,g3)
    c: Coincident(g3,g0)
    c: Horizontal(g0)
    c: Horizontal(g2)
    c: Vertical(g1)
    c: Vertical(g3)
    c: Symmetric(g2,g0,g4)
    c: Distance(g1,g3) = 1.5
    c: Distance(g0,g2) = 5.3
    c: Coincident(g4,g-1)
    c: Horizontal(g5)
    c: Coincident(g6,g5)
    c: PointOnObject(g6,g-2)
    c: Coincident(g7,g6)
    c: Coincident(g7,g5)
    c: Equal(g7,g6)
    c: Equal(g2,g5)
    c: Vertical(g5,g2)
    c: DistanceY(g1,g5) = 1
    c: DistanceY(g5,g6) = 3
    c: Perpendicular(g7,g5)
    c: PointOnObject(g8,g1)
    c: PointOnObject(g8,g-1)
    c: Coincident(g9,g10)
    c: Coincident(g10,g11)
    c: Coincident(g11,g12)
    c: Coincident(g12,g9)
    c: Vertical(g9)
    c: Vertical(g11)
    c: Horizontal(g10)
    c: Horizontal(g12)
    c: Symmetric(g11,g9,g13)
    c: Coincident(g13,g4)
    c: PointOnObject(g10,g1)
    c: Equal(g11,g12)
FEATURE [PartDesign::Pocket] Pocket008
  BaseFeature = -> Revolution008
  Direction = (0,0,-1)
  Length = 2
  Length2 = 5
  Placement = pos=(0,0,0) rot=(1,0,0;1.5708rad)
  Profile = -> Sketch017
  ReferenceAxis = -> Sketch017 [N_Axis]
  Refine = true
  Suppressed = false
  Type = 0
FEATURE [PartDesign::Body] Body008
  AllowCompound = false
  Group = -> [Sketch016,Revolution008,Sketch017,Pocket008]
  Origin = -> Origin017
  Tip = -> Pocket008
FEATURE [Part::Cut] Cut008
  Base = -> Body008
  Refine = true
  Tool = -> Extrude008
FEATURE [PartDesign::CoordinateSystem] Next008
  AttacherType = Attacher::AttachEngine3D
  AttachmentOffset = pos=(-20,0,0) rot=(0,0,1;3.14159rad)
  AttachmentSupport = -> [Cut008]
  MapMode = 11
  Placement = pos=(-4.2e-15,20,0) rot=(0,0,1;1.5708rad)
  expr: .AttachmentOffset.Base.x = -<<Spreadsheet>>.LineupDistance
FEATURE [PartDesign::CoordinateSystem] This008
  AttacherType = Attacher::AttachEngine3D
  AttachmentOffset = pos=(0,0,0) rot=(0,0,1;3.14159rad)
  AttachmentSupport = -> [Cut008]
  MapMode = 11
  Placement = pos=(2e-16,0,0) rot=(0,0,1;1.5708rad)
FEATURE [App::Part] Part007  label="9 - Square"
  Group = -> [LCS_Origin009,Body008,ShapeString008,Extrude008,Cut008,This008,Next008]
  Origin = -> Origin018
FEATURE [App::Link] ____Square  label="9 - Square001"
  AttachedBy = #This008
  AttachedTo = ____Triangle#Next007
  LinkPlacement = pos=(60,-40,0) rot=(0,0,-1;1.5708rad)
  LinkedObject = -> Part007
  Placement = pos=(60,-40,0) rot=(0,0,-1;1.5708rad)
  SolverId = Asm4EE
  expr: Placement = ____Triangle.Placement * Next007.Placement * AttachmentOffset * This008.Placement ^ -1
FEATURE [PartDesign::CoordinateSystem] LCS_Origin010
  AttacherType = Attacher::AttachEngine3D
  AttachmentSupport = -> [X_Axis020]
  MapMode = 2
FEATURE [Part::Part2DObjectPython] ShapeString009  # Draft 2D object (typed FeaturePython)
  FontFile = <userpath>/.fonts/ttf/arial.ttf
  Fuse = false
  Justification = 6
  JustificationReference = 0
  KeepLeftMargin = false
  MakeFace = true
  ObliqueAngle = 0
  ScaleToSize = true
  Size = 3
  String = 10
  Tracking = 0
FEATURE [Part::Extrusion] Extrude009  label="Text009"
  Base = -> ShapeString009
  Dir = (0,0,1)
  DirMode = 2
  FaceMakerClass = Part::FaceMakerBullseye
  FaceMakerMode = 3
  LengthFwd = 2
  LengthRev = 0
  Placement = pos=(1.5,3,43) rot=(0,0,1;1.5708rad)
  Solid = false
  Symmetric = false
FEATURE [Sketcher::SketchObject] Sketch018
  ArcFitTolerance = 1e-06
  AttachmentSupport = -> [XZ_Plane019]
  FullyConstrained = true
  MakeInternals = false
  MapMode = 5
  Placement = pos=(0,0,0) rot=(1,0,0;1.5708rad)
  expr: Constraints[10] = <<Spreadsheet>>.TopFlatDiameter / 2
  expr: Constraints[22] = <<Spreadsheet>>.TopRadius
  expr: Constraints[23] = <<Spreadsheet>>.BottomRadius1
  expr: Constraints[24] = <<Spreadsheet>>.BottomRadius2
  expr: Constraints[25] = <<Spreadsheet>>.BottomToStraightHeight
  expr: Constraints[26] = <<Spreadsheet>>.BottomFlatDiameter / 2
  expr: Constraints[27] = <<Spreadsheet>>.BottomRadius3
  expr: Constraints[5] = <<Spreadsheet>>.HoleDiameter / 2
  expr: Constraints[6] = <<Spreadsheet>>.HoleDepth
  expr: Constraints[7] = <<Spreadsheet>>.TopSolidLength
  sketch-geometry (10):
    g0: LineSegment StartX=-1.9 StartY=0 StartZ=0 EndX=-1.9 EndY=35 EndZ=0
    g1: LineSegment StartX=-1.9 StartY=35 StartZ=0 EndX=0 EndY=35 EndZ=0
    g2: LineSegment StartX=0 StartY=35 StartZ=0 EndX=0 EndY=45 EndZ=0
    g3: LineSegment StartX=0 StartY=45 StartZ=0 EndX=-3 EndY=45 EndZ=0
    g4: ArcOfCircle CenterX=-3 CenterY=40 CenterZ=0 NormalX=0 NormalY=0 NormalZ=1 AngleXU=0 Radius=5 StartAngle=1.5708 EndAngle=3.19395
    g5: LineSegment StartX=-1.9 StartY=0 StartZ=0 EndX=-3.5 EndY=0 EndZ=0
    g6: ArcOfCircle CenterX=-3.5 CenterY=3 CenterZ=0 NormalX=0 NormalY=0 NormalZ=1 AngleXU=0 Radius=3 StartAngle=3.70042 EndAngle=4.71239
    g7: ArcOfCircle CenterX=0.739385 CenterY=5.65096 CenterZ=0 NormalX=0 NormalY=0 NormalZ=1 AngleXU=0 Radius=8 StartAngle=2.75061 EndAngle=3.70042
    g8: ArcOfCircle CenterX=-9.43052 CenterY=9.84299 CenterZ=0 NormalX=0 NormalY=0 NormalZ=1 AngleXU=0 Radius=3 StartAngle=5.89221 EndAngle=6.33555
    g9: LineSegment StartX=-6.43463 StartY=10 StartZ=0 EndX=-7.99315 EndY=39.7383 EndZ=0
  constraints (28):
    c: PointOnObject(g0,g-1)
    c: Vertical(g0)
    c: Coincident(g0,g1)
    c: PointOnObject(g1,g-2)
    c: Horizontal(g1)
    c: DistanceX(g1,g1) = 1.9
    c: DistanceY(g0,g0) = 35
    c: Distance(g2) = 10
    c: Coincident(g2,g1)
    c: PointOnObject(g2,g-2)
    c: Distance(g3) = 3
    c: Coincident(g3,g2)
    c: Horizontal(g3)
    c: Coincident(g5,g0)
    c: PointOnObject(g5,g-1)
    c: Tangent(g6,g5) = 1.5708
    c: Tangent(g7,g6) = -1.5708
    c: Tangent(g8,g7) = 1.5708
    c: Tangent(g9,g8) = -1.5708
    c: Tangent(g4,g3) = -1.5708
    c: Tangent(g9,g4) = 1.5708
    c: Angle(g-2,g9) = 0.0523599
    c: Radius(g4) = 5
    c: Radius(g6) = 3
    c: Radius(g7) = 8
    c: DistanceY(g8) = 10
    c: DistanceX(g5,g-1) = 3.5
    c: Radius(g8) = 3
FEATURE [PartDesign::Revolution] Revolution009
  Angle = 360
  Angle2 = 60
  Axis = (0,2e-16,1)
  Base = (0,0,0)
  Placement = pos=(0,0,0) rot=(1,0,0;1.5708rad)
  Profile = -> Sketch018
  ReferenceAxis = -> Sketch018 [V_Axis]
  Refine = true
  Suppressed = false
  Type = 0
FEATURE [Sketcher::SketchObject] Sketch019
  ArcFitTolerance = 1e-06
  AttachmentSupport = -> [Revolution009]
  FullyConstrained = true
  MakeInternals = false
  MapMode = 5
  Placement = pos=(0,1e-14,45) rot=(0,0,1;3.14159rad)
  sketch-geometry (12):
    g0: LineSegment [constr] StartX=-0.75 StartY=-2.65 StartZ=0 EndX=0.75 EndY=-2.65 EndZ=0
    g1: LineSegment [constr] StartX=0.75 StartY=-2.65 StartZ=0 EndX=0.75 EndY=2.65 EndZ=0
    g2: LineSegment [constr] StartX=0.75 StartY=2.65 StartZ=0 EndX=-0.75 EndY=2.65 EndZ=0
    g3: LineSegment [constr] StartX=-0.75 StartY=2.65 StartZ=0 EndX=-0.75 EndY=-2.65 EndZ=0
    g4: GeomPoint [constr] X=0 Y=0 Z=0
    g5: LineSegment StartX=-0.75 StartY=3.65 StartZ=0 EndX=0.75 EndY=3.65 EndZ=0
    g6: ArcOfCircle CenterX=5.625 CenterY=3.65 CenterZ=0 NormalX=0 NormalY=0 NormalZ=1 AngleXU=0 Radius=6.375 StartAngle=2.65164 EndAngle=3.14159
    g7: ArcOfCircle CenterX=-5.625 CenterY=3.65 CenterZ=0 NormalX=0 NormalY=0 NormalZ=1 AngleXU=0 Radius=6.375 StartAngle=0 EndAngle=0.489957
    g8: GeomPoint X=0.75 Y=0 Z=0
    g9: GeomPoint [constr] X=0 Y=0 Z=0
    g10: ArcOfCircle CenterX=-2.34083 CenterY=0 CenterZ=0 NormalX=0 NormalY=0 NormalZ=1 AngleXU=0 Radius=3.09083 StartAngle=5.25304 EndAngle=7.31333
    g11: LineSegment StartX=-0.75 StartY=-2.65 StartZ=0 EndX=-0.75 EndY=2.65 EndZ=0
  constraints (32):
    c: Coincident(g0,g1)
    c: Coincident(g1,g2)
    c: Coincident(g2,g3)
    c: Coincident(g3,g0)
    c: Horizontal(g0)
    c: Horizontal(g2)
    c: Vertical(g1)
    c: Vertical(g3)
    c: Symmetric(g2,g0,g4)
    c: Distance(g1,g3) = 1.5
    c: Distance(g0,g2) = 5.3
    c: Coincident(g4,g-1)
    c: Horizontal(g5)
    c: Coincident(g6,g5)
    c: PointOnObject(g6,g-2)
    c: Coincident(g7,g6)
    c: Coincident(g7,g5)
    c: Equal(g7,g6)
    c: Equal(g2,g5)
    c: Vertical(g5,g2)
    c: DistanceY(g1,g5) = 1
    c: DistanceY(g5,g6) = 3
    c: Perpendicular(g7,g5)
    c: PointOnObject(g8,g1)
    c: PointOnObject(g8,g-1)
    c: Coincident(g9,g4)
    c: PointOnObject(g10,g3)
    c: PointOnObject(g8,g10)
    c: PointOnObject(g10,g-1)
    c: Coincident(g11,g10)
    c: Coincident(g11,g10)
    c: Coincident(g10,g2)
FEATURE [PartDesign::Pocket] Pocket009
  BaseFeature = -> Revolution009
  Direction = (0,0,-1)
  Length = 2
  Length2 = 5
  Placement = pos=(0,0,0) rot=(1,0,0;1.5708rad)
  Profile = -> Sketch019
  ReferenceAxis = -> Sketch019 [N_Axis]
  Refine = true
  Suppressed = false
  Type = 0
FEATURE [PartDesign::Body] Body009
  AllowCompound = false
  Group = -> [Sketch018,Revolution009,Sketch019,Pocket009]
  Origin = -> Origin019
  Tip = -> Pocket009
FEATURE [Part::Cut] Cut009
  Base = -> Body009
  Refine = true
  Tool = -> Extrude009
FEATURE [PartDesign::CoordinateSystem] Next009
  AttacherType = Attacher::AttachEngine3D
  AttachmentOffset = pos=(-20,0,0) rot=(0,0,1;3.14159rad)
  AttachmentSupport = -> [Cut009]
  MapMode = 11
  Placement = pos=(-4.2e-15,20,0) rot=(0,0,1;1.5708rad)
  expr: .AttachmentOffset.Base.x = -<<Spreadsheet>>.LineupDistance
FEATURE [PartDesign::CoordinateSystem] This009
  AttacherType = Attacher::AttachEngine3D
  AttachmentOffset = pos=(0,0,0) rot=(0,0,1;3.14159rad)
  AttachmentSupport = -> [Cut009]
  MapMode = 11
  Placement = pos=(2e-16,0,0) rot=(0,0,1;1.5708rad)
FEATURE [App::Part] Part008  label="10 - Half Round"
  Group = -> [LCS_Origin010,Body009,ShapeString009,Extrude009,Cut009,This009,Next009]
  Origin = -> Origin020
FEATURE [App::Link] _0___Half_Round  label="10 - Half Round001"
  AttachedBy = #This009
  AttachedTo = ____Square#Next008
  LinkPlacement = pos=(80,-40,0) rot=(0,0,-1;1.5708rad)
  LinkedObject = -> Part008
  Placement = pos=(80,-40,0) rot=(0,0,-1;1.5708rad)
  SolverId = Asm4EE
  expr: Placement = ____Square.Placement * Next008.Placement * AttachmentOffset * This009.Placement ^ -1
FEATURE [PartDesign::CoordinateSystem] LCS_Origin011
  AttacherType = Attacher::AttachEngine3D
  AttachmentSupport = -> [X_Axis022]
  MapMode = 2
FEATURE [Part::Part2DObjectPython] ShapeString010  # Draft 2D object (typed FeaturePython)
  FontFile = <userpath>/.fonts/ttf/arial.ttf
  Fuse = false
  Justification = 6
  JustificationReference = 0
  KeepLeftMargin = false
  MakeFace = true
  ObliqueAngle = 0
  ScaleToSize = true
  Size = 3
  String = 1
  Tracking = 0
FEATURE [Part::Extrusion] Extrude010  label="Text010"
  Base = -> ShapeString010
  Dir = (0,0,1)
  DirMode = 2
  FaceMakerClass = Part::FaceMakerBullseye
  FaceMakerMode = 3
  LengthFwd = 2
  LengthRev = 0
  Placement = pos=(1.5,4,43) rot=(0,0,1;1.5708rad)
  Solid = false
  Symmetric = false
FEATURE [Sketcher::SketchObject] Sketch020
  ArcFitTolerance = 1e-06
  AttachmentSupport = -> [XZ_Plane021]
  FullyConstrained = true
  MakeInternals = false
  MapMode = 5
  Placement = pos=(0,0,0) rot=(1,0,0;1.5708rad)
  expr: Constraints[10] = <<Spreadsheet>>.TopFlatDiameter / 2
  expr: Constraints[22] = <<Spreadsheet>>.TopRadius
  expr: Constraints[23] = <<Spreadsheet>>.BottomRadius1
  expr: Constraints[24] = <<Spreadsheet>>.BottomRadius2
  expr: Constraints[25] = <<Spreadsheet>>.BottomToStraightHeight
  expr: Constraints[26] = <<Spreadsheet>>.BottomFlatDiameter / 2
  expr: Constraints[27] = <<Spreadsheet>>.BottomRadius3
  expr: Constraints[5] = <<Spreadsheet>>.HoleDiameter / 2
  expr: Constraints[6] = <<Spreadsheet>>.HoleDepth
  expr: Constraints[7] = <<Spreadsheet>>.TopSolidLength
  sketch-geometry (10):
    g0: LineSegment StartX=-1.9 StartY=0 StartZ=0 EndX=-1.9 EndY=35 EndZ=0
    g1: LineSegment StartX=-1.9 StartY=35 StartZ=0 EndX=0 EndY=35 EndZ=0
    g2: LineSegment StartX=0 StartY=35 StartZ=0 EndX=0 EndY=45 EndZ=0
    g3: LineSegment StartX=0 StartY=45 StartZ=0 EndX=-3 EndY=45 EndZ=0
    g4: ArcOfCircle CenterX=-3 CenterY=40 CenterZ=0 NormalX=0 NormalY=0 NormalZ=1 AngleXU=0 Radius=5 StartAngle=1.5708 EndAngle=3.19395
    g5: LineSegment StartX=-1.9 StartY=0 StartZ=0 EndX=-3.5 EndY=0 EndZ=0
    g6: ArcOfCircle CenterX=-3.5 CenterY=3 CenterZ=0 NormalX=0 NormalY=0 NormalZ=1 AngleXU=0 Radius=3 StartAngle=3.70042 EndAngle=4.71239
    g7: ArcOfCircle CenterX=0.739385 CenterY=5.65096 CenterZ=0 NormalX=0 NormalY=0 NormalZ=1 AngleXU=0 Radius=8 StartAngle=2.75061 EndAngle=3.70042
    g8: ArcOfCircle CenterX=-9.43052 CenterY=9.84299 CenterZ=0 NormalX=0 NormalY=0 NormalZ=1 AngleXU=0 Radius=3 StartAngle=5.89221 EndAngle=6.33555
    g9: LineSegment StartX=-6.43463 StartY=10 StartZ=0 EndX=-7.99315 EndY=39.7383 EndZ=0
  constraints (28):
    c: PointOnObject(g0,g-1)
    c: Vertical(g0)
    c: Coincident(g0,g1)
    c: PointOnObject(g1,g-2)
    c: Horizontal(g1)
    c: DistanceX(g1,g1) = 1.9
    c: DistanceY(g0,g0) = 35
    c: Distance(g2) = 10
    c: Coincident(g2,g1)
    c: PointOnObject(g2,g-2)
    c: Distance(g3) = 3
    c: Coincident(g3,g2)
    c: Horizontal(g3)
    c: Coincident(g5,g0)
    c: PointOnObject(g5,g-1)
    c: Tangent(g6,g5) = 1.5708
    c: Tangent(g7,g6) = -1.5708
    c: Tangent(g8,g7) = 1.5708
    c: Tangent(g9,g8) = -1.5708
    c: Tangent(g4,g3) = -1.5708
    c: Tangent(g9,g4) = 1.5708
    c: Angle(g-2,g9) = 0.0523599
    c: Radius(g4) = 5
    c: Radius(g6) = 3
    c: Radius(g7) = 8
    c: DistanceY(g8) = 10
    c: DistanceX(g5,g-1) = 3.5
    c: Radius(g8) = 3
FEATURE [PartDesign::Revolution] Revolution010
  Angle = 360
  Angle2 = 60
  Axis = (0,2e-16,1)
  Base = (0,0,0)
  Placement = pos=(0,0,0) rot=(1,0,0;1.5708rad)
  Profile = -> Sketch020
  ReferenceAxis = -> Sketch020 [V_Axis]
  Refine = true
  Suppressed = false
  Type = 0
FEATURE [Sketcher::SketchObject] Sketch021
  ArcFitTolerance = 1e-06
  AttachmentSupport = -> [Revolution010]
  FullyConstrained = true
  MakeInternals = false
  MapMode = 5
  Placement = pos=(0,1e-14,45) rot=(0,0,1;3.14159rad)
  sketch-geometry (8):
    g0: LineSegment StartX=-0.75 StartY=-2.65 StartZ=0 EndX=0.75 EndY=-2.65 EndZ=0
    g1: LineSegment StartX=0.75 StartY=-2.65 StartZ=0 EndX=0.75 EndY=2.65 EndZ=0
    g2: LineSegment StartX=0.75 StartY=2.65 StartZ=0 EndX=-0.75 EndY=2.65 EndZ=0
    g3: LineSegment StartX=-0.75 StartY=2.65 StartZ=0 EndX=-0.75 EndY=-2.65 EndZ=0
    g4: GeomPoint [constr] X=0 Y=0 Z=0
    g5: LineSegment StartX=-0.75 StartY=3.65 StartZ=0 EndX=0.75 EndY=3.65 EndZ=0
    g6: ArcOfCircle CenterX=5.625 CenterY=3.65 CenterZ=0 NormalX=0 NormalY=0 NormalZ=1 AngleXU=0 Radius=6.375 StartAngle=2.65164 EndAngle=3.14159
    g7: ArcOfCircle CenterX=-5.625 CenterY=3.65 CenterZ=0 NormalX=0 NormalY=0 NormalZ=1 AngleXU=0 Radius=6.375 StartAngle=0 EndAngle=0.489957
  constraints (23):
    c: Coincident(g0,g1)
    c: Coincident(g1,g2)
    c: Coincident(g2,g3)
    c: Coincident(g3,g0)
    c: Horizontal(g0)
    c: Horizontal(g2)
    c: Vertical(g1)
    c: Vertical(g3)
    c: Symmetric(g2,g0,g4)
    c: Distance(g1,g3) = 1.5
    c: Distance(g0,g2) = 5.3
    c: Coincident(g4,g-1)
    c: Horizontal(g5)
    c: Coincident(g6,g5)
    c: PointOnObject(g6,g-2)
    c: Coincident(g7,g6)
    c: Coincident(g7,g5)
    c: Equal(g7,g6)
    c: Equal(g2,g5)
    c: Vertical(g5,g2)
    c: DistanceY(g1,g5) = 1
    c: DistanceY(g5,g6) = 3
    c: Perpendicular(g7,g5)
FEATURE [PartDesign::Pocket] Pocket010
  BaseFeature = -> Revolution010
  Direction = (0,0,-1)
  Length = 2
  Length2 = 5
  Placement = pos=(0,0,0) rot=(1,0,0;1.5708rad)
  Profile = -> Sketch021
  ReferenceAxis = -> Sketch021 [N_Axis]
  Refine = true
  Suppressed = false
  Type = 0
FEATURE [PartDesign::Body] Body010
  AllowCompound = false
  Group = -> [Sketch020,Revolution010,Sketch021,Pocket010]
  Origin = -> Origin021
  Tip = -> Pocket010
FEATURE [Part::Cut] Cut010
  Base = -> Body010
  Refine = true
  Tool = -> Extrude010
FEATURE [PartDesign::CoordinateSystem] Next010
  AttacherType = Attacher::AttachEngine3D
  AttachmentOffset = pos=(-20,0,0) rot=(0,0,1;3.14159rad)
  AttachmentSupport = -> [Cut010]
  MapMode = 11
  Placement = pos=(-4.2e-15,20,0) rot=(0,0,1;1.5708rad)
  expr: .AttachmentOffset.Base.x = -<<Spreadsheet>>.LineupDistance
FEATURE [PartDesign::CoordinateSystem] This010
  AttacherType = Attacher::AttachEngine3D
  AttachmentOffset = pos=(0,0,0) rot=(0,0,1;3.14159rad)
  AttachmentSupport = -> [Cut010]
  MapMode = 11
  Placement = pos=(2e-16,0,0) rot=(0,0,1;1.5708rad)
FEATURE [App::Part] Part009  label="1 - Flat Pointy"
  Group = -> [LCS_Origin011,Body010,ShapeString010,Extrude010,Cut010,This010,Next010]
  Origin = -> Origin022
FEATURE [PartDesign::CoordinateSystem] LCS_Origin012
  AttacherType = Attacher::AttachEngine3D
  AttachmentSupport = -> [X_Axis024]
  MapMode = 2
FEATURE [Part::Part2DObjectPython] ShapeString011  # Draft 2D object (typed FeaturePython)
  FontFile = <userpath>/.fonts/ttf/arial.ttf
  Fuse = false
  Justification = 6
  JustificationReference = 0
  KeepLeftMargin = false
  MakeFace = true
  ObliqueAngle = 0
  ScaleToSize = true
  Size = 3
  String = 2
  Tracking = 0
FEATURE [Part::Extrusion] Extrude011  label="Text011"
  Base = -> ShapeString011
  Dir = (0,0,1)
  DirMode = 2
  FaceMakerClass = Part::FaceMakerBullseye
  FaceMakerMode = 3
  LengthFwd = 2
  LengthRev = 0
  Placement = pos=(1.5,4,43) rot=(0,0,1;1.5708rad)
  Solid = false
  Symmetric = false
FEATURE [Sketcher::SketchObject] Sketch022
  ArcFitTolerance = 1e-06
  AttachmentSupport = -> [XZ_Plane023]
  FullyConstrained = true
  MakeInternals = false
  MapMode = 5
  Placement = pos=(0,0,0) rot=(1,0,0;1.5708rad)
  expr: Constraints[10] = <<Spreadsheet>>.TopFlatDiameter / 2
  expr: Constraints[22] = <<Spreadsheet>>.TopRadius
  expr: Constraints[23] = <<Spreadsheet>>.BottomRadius1
  expr: Constraints[24] = <<Spreadsheet>>.BottomRadius2
  expr: Constraints[25] = <<Spreadsheet>>.BottomToStraightHeight
  expr: Constraints[26] = <<Spreadsheet>>.BottomFlatDiameter / 2
  expr: Constraints[27] = <<Spreadsheet>>.BottomRadius3
  expr: Constraints[5] = <<Spreadsheet>>.HoleDiameter / 2
  expr: Constraints[6] = <<Spreadsheet>>.HoleDepth
  expr: Constraints[7] = <<Spreadsheet>>.TopSolidLength
  sketch-geometry (10):
    g0: LineSegment StartX=-1.9 StartY=0 StartZ=0 EndX=-1.9 EndY=35 EndZ=0
    g1: LineSegment StartX=-1.9 StartY=35 StartZ=0 EndX=0 EndY=35 EndZ=0
    g2: LineSegment StartX=0 StartY=35 StartZ=0 EndX=0 EndY=45 EndZ=0
    g3: LineSegment StartX=0 StartY=45 StartZ=0 EndX=-3 EndY=45 EndZ=0
    g4: ArcOfCircle CenterX=-3 CenterY=40 CenterZ=0 NormalX=0 NormalY=0 NormalZ=1 AngleXU=0 Radius=5 StartAngle=1.5708 EndAngle=3.19395
    g5: LineSegment StartX=-1.9 StartY=0 StartZ=0 EndX=-3.5 EndY=0 EndZ=0
    g6: ArcOfCircle CenterX=-3.5 CenterY=3 CenterZ=0 NormalX=0 NormalY=0 NormalZ=1 AngleXU=0 Radius=3 StartAngle=3.70042 EndAngle=4.71239
    g7: ArcOfCircle CenterX=0.739385 CenterY=5.65096 CenterZ=0 NormalX=0 NormalY=0 NormalZ=1 AngleXU=0 Radius=8 StartAngle=2.75061 EndAngle=3.70042
    g8: ArcOfCircle CenterX=-9.43052 CenterY=9.84299 CenterZ=0 NormalX=0 NormalY=0 NormalZ=1 AngleXU=0 Radius=3 StartAngle=5.89221 EndAngle=6.33555
    g9: LineSegment StartX=-6.43463 StartY=10 StartZ=0 EndX=-7.99315 EndY=39.7383 EndZ=0
  constraints (28):
    c: PointOnObject(g0,g-1)
    c: Vertical(g0)
    c: Coincident(g0,g1)
    c: PointOnObject(g1,g-2)
    c: Horizontal(g1)
    c: DistanceX(g1,g1) = 1.9
    c: DistanceY(g0,g0) = 35
    c: Distance(g2) = 10
    c: Coincident(g2,g1)
    c: PointOnObject(g2,g-2)
    c: Distance(g3) = 3
    c: Coincident(g3,g2)
    c: Horizontal(g3)
    c: Coincident(g5,g0)
    c: PointOnObject(g5,g-1)
    c: Tangent(g6,g5) = 1.5708
    c: Tangent(g7,g6) = -1.5708
    c: Tangent(g8,g7) = 1.5708
    c: Tangent(g9,g8) = -1.5708
    c: Tangent(g4,g3) = -1.5708
    c: Tangent(g9,g4) = 1.5708
    c: Angle(g-2,g9) = 0.0523599
    c: Radius(g4) = 5
    c: Radius(g6) = 3
    c: Radius(g7) = 8
    c: DistanceY(g8) = 10
    c: DistanceX(g5,g-1) = 3.5
    c: Radius(g8) = 3
FEATURE [PartDesign::Revolution] Revolution011
  Angle = 360
  Angle2 = 60
  Axis = (0,2e-16,1)
  Base = (0,0,0)
  Placement = pos=(0,0,0) rot=(1,0,0;1.5708rad)
  Profile = -> Sketch022
  ReferenceAxis = -> Sketch022 [V_Axis]
  Refine = true
  Suppressed = false
  Type = 0
FEATURE [Sketcher::SketchObject] Sketch023
  ArcFitTolerance = 1e-06
  AttachmentSupport = -> [Revolution011]
  FullyConstrained = true
  MakeInternals = false
  MapMode = 5
  Placement = pos=(0,1e-14,45) rot=(0,0,1;3.14159rad)
  sketch-geometry (9):
    g0: LineSegment StartX=-0.75 StartY=-2.65 StartZ=0 EndX=0.75 EndY=-2.65 EndZ=0
    g1: LineSegment StartX=0.75 StartY=-2.65 StartZ=0 EndX=0.75 EndY=2.65 EndZ=0
    g2: LineSegment StartX=0.75 StartY=2.65 StartZ=0 EndX=-0.75 EndY=2.65 EndZ=0
    g3: LineSegment StartX=-0.75 StartY=2.65 StartZ=0 EndX=-0.75 EndY=-2.65 EndZ=0
    g4: GeomPoint [constr] X=0 Y=0 Z=0
    g5: LineSegment StartX=-0.75 StartY=3.65 StartZ=0 EndX=0.75 EndY=3.65 EndZ=0
    g6: LineSegment StartX=-0.75 StartY=3.65 StartZ=0 EndX=-0.75 EndY=6.65 EndZ=0
    g7: LineSegment StartX=-0.75 StartY=6.65 StartZ=0 EndX=0.75 EndY=6.65 EndZ=0
    g8: LineSegment StartX=0.75 StartY=6.65 StartZ=0 EndX=0.75 EndY=3.65 EndZ=0
  constraints (24):
    c: Coincident(g0,g1)
    c: Coincident(g1,g2)
    c: Coincident(g2,g3)
    c: Coincident(g3,g0)
    c: Horizontal(g0)
    c: Horizontal(g2)
    c: Vertical(g1)
    c: Vertical(g3)
    c: Symmetric(g2,g0,g4)
    c: Distance(g1,g3) = 1.5
    c: Distance(g0,g2) = 5.3
    c: Coincident(g4,g-1)
    c: Horizontal(g5)
    c: Equal(g2,g5)
    c: Vertical(g5,g2)
    c: DistanceY(g1,g5) = 1
    c: Coincident(g5,g6)
    c: Vertical(g6)
    c: Coincident(g6,g7)
    c: Horizontal(g7)
    c: Coincident(g7,g8)
    c: Coincident(g8,g5)
    c: Vertical(g8)
    c: DistanceY(g6,g6) = 3
FEATURE [PartDesign::Pocket] Pocket011
  BaseFeature = -> Revolution011
  Direction = (0,0,-1)
  Length = 2
  Length2 = 5
  Placement = pos=(0,0,0) rot=(1,0,0;1.5708rad)
  Profile = -> Sketch023
  ReferenceAxis = -> Sketch023 [N_Axis]
  Refine = true
  Suppressed = false
  Type = 0
FEATURE [PartDesign::Body] Body011
  AllowCompound = false
  Group = -> [Sketch022,Revolution011,Sketch023,Pocket011]
  Origin = -> Origin023
  Tip = -> Pocket011
FEATURE [Part::Cut] Cut011
  Base = -> Body011
  Refine = true
  Tool = -> Extrude011
FEATURE [PartDesign::CoordinateSystem] Next011
  AttacherType = Attacher::AttachEngine3D
  AttachmentOffset = pos=(-20,0,0) rot=(0,0,1;3.14159rad)
  AttachmentSupport = -> [Cut011]
  MapMode = 11
  Placement = pos=(-4.2e-15,20,0) rot=(0,0,1;1.5708rad)
  expr: .AttachmentOffset.Base.x = -<<Spreadsheet>>.LineupDistance
FEATURE [PartDesign::CoordinateSystem] This011
  AttacherType = Attacher::AttachEngine3D
  AttachmentOffset = pos=(0,0,0) rot=(0,0,1;3.14159rad)
  AttachmentSupport = -> [Cut011]
  MapMode = 11
  Placement = pos=(2e-16,0,0) rot=(0,0,1;1.5708rad)
FEATURE [App::Part] Part010  label="2 - Flat Straight"
  Group = -> [LCS_Origin012,Body011,ShapeString011,Extrude011,Cut011,This011,Next011]
  Origin = -> Origin024
FEATURE [App::DocumentObjectGroup] Parts
  Group = -> [Part001,Part002,Part003,Part004,Part005,Part006,Part007,Part008,Part009,Part010]
FEATURE [App::Link] ____Flat_Pointy  label="1 - Flat Pointy001"
  AttachedBy = #This010
  AttachedTo = Parent Assembly#LCS_Origin
  AttachmentOffset = pos=(0,-20,0) rot=(0,0,1;0rad)
  LinkPlacement = pos=(0,-20,0) rot=(0,0,-1;1.5708rad)
  LinkedObject = -> Part009
  Placement = pos=(0,-20,0) rot=(0,0,-1;1.5708rad)
  SolverId = Asm4EE
  expr: Placement = LCS_Origin.Placement * AttachmentOffset * This010.Placement ^ -1
FEATURE [App::Link] ____Flat_Straight  label="2 - Flat Straight001"
  AttachedBy = #This011
  AttachedTo = ____Flat_Pointy#Next010
  LinkPlacement = pos=(20,-20,0) rot=(0,0,-1;1.5708rad)
  LinkedObject = -> Part010
  Placement = pos=(20,-20,0) rot=(0,0,-1;1.5708rad)
  SolverId = Asm4EE
  expr: Placement = ____Flat_Pointy.Placement * Next010.Placement * AttachmentOffset * This011.Placement ^ -1
FEATURE [App::Part] Assembly  label="Lineup"
  AssemblyType = Part::Link
  Group = -> [LCS_Origin,Constraints,Variables,Configurations,____Knife_Rounded,____Knife_Rounded_Small,____Triangle_Flattened,____Sharp_Edge,____Round,____Triangle,____Square,_0___Half_Round,____Flat_Pointy,____Flat_Straight]
  Origin = -> Origin002
  Type = Assembly
